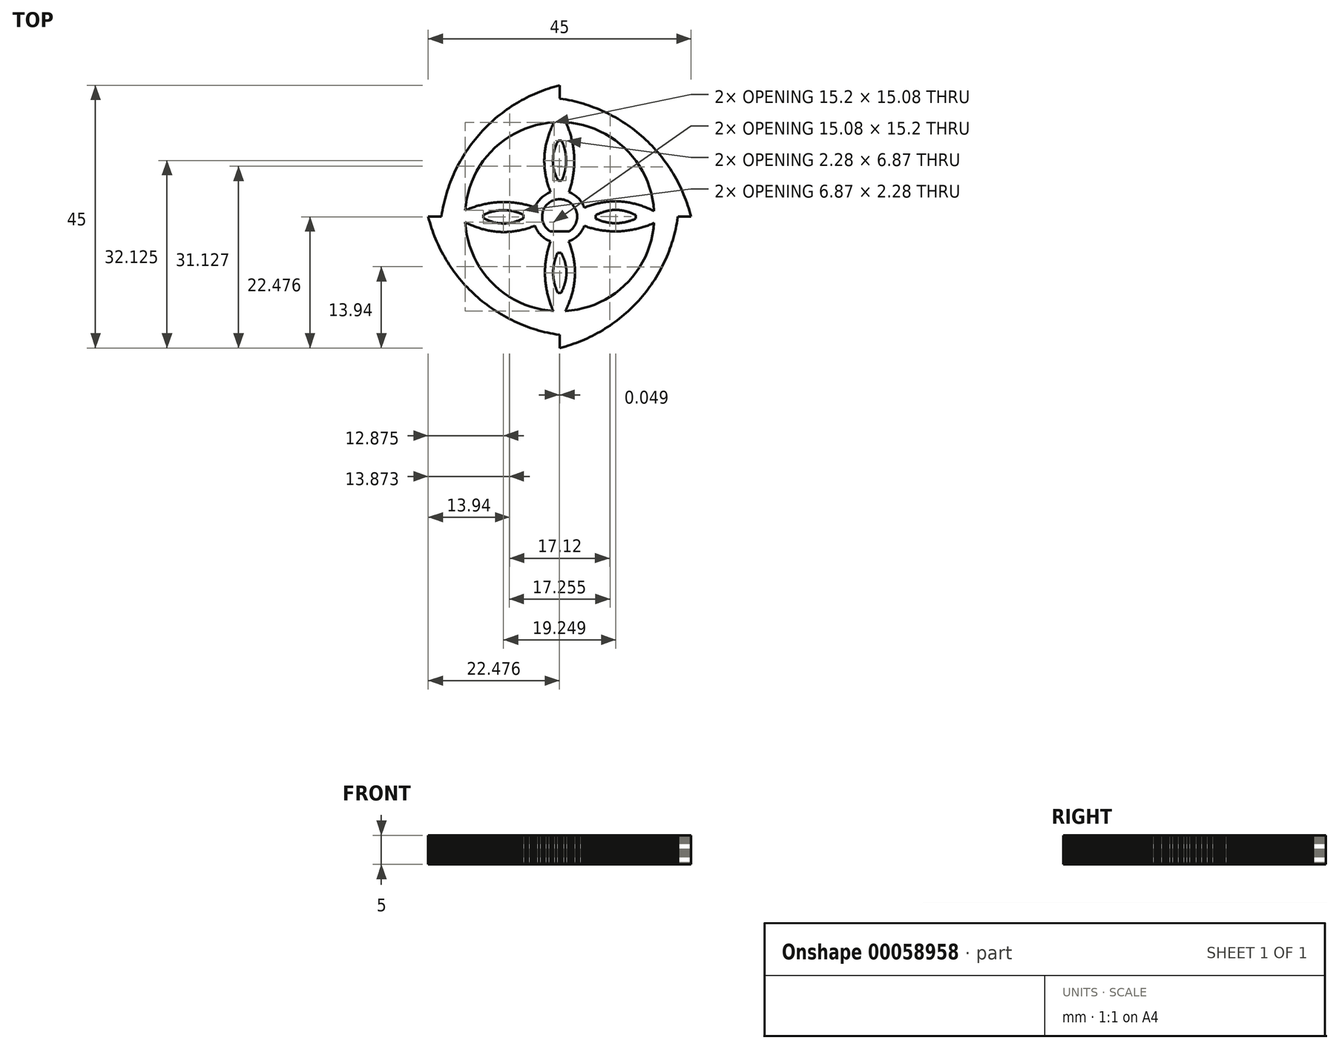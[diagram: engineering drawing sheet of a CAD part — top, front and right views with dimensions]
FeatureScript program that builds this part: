
annotation { "Feature Type Name" : "Feature", "Feature Type Description" : "" }
export const myFeature = defineFeature(function(context is Context, id is Id, definition is map)
    precondition{}
    {
        {
            var Q0;
            Q0=qCreatedBy(makeId("Top.planeOp"),FACE);
            var sketch = newSketch(context, id + "F0", { "sketchPlane" : qUnion([Q0])});
            skLineSegment(sketch, "E0", {"start": v(0, 22.5) * mm, "end": v(-0.48, 22.37) * mm});
            skLineSegment(sketch, "E1", {"start": v(-0.48, 22.37) * mm, "end": v(-0.97, 22.24) * mm});
            skLineSegment(sketch, "E2", {"start": v(-0.97, 22.24) * mm, "end": v(-1.44, 22.1) * mm});
            skLineSegment(sketch, "E3", {"start": v(-1.44, 22.1) * mm, "end": v(-1.92, 21.94) * mm});
            skLineSegment(sketch, "E4", {"start": v(-1.92, 21.94) * mm, "end": v(-2.4, 21.78) * mm});
            skLineSegment(sketch, "E5", {"start": v(-2.4, 21.78) * mm, "end": v(-2.86, 21.61) * mm});
            skLineSegment(sketch, "E6", {"start": v(-2.86, 21.61) * mm, "end": v(-3.33, 21.43) * mm});
            skLineSegment(sketch, "E7", {"start": v(-3.33, 21.43) * mm, "end": v(-3.8, 21.24) * mm});
            skLineSegment(sketch, "E8", {"start": v(-3.8, 21.24) * mm, "end": v(-4.25, 21.05) * mm});
            skLineSegment(sketch, "E9", {"start": v(-4.25, 21.05) * mm, "end": v(-4.71, 20.84) * mm});
            skLineSegment(sketch, "E10", {"start": v(-4.71, 20.84) * mm, "end": v(-5.16, 20.63) * mm});
            skLineSegment(sketch, "E11", {"start": v(-5.16, 20.63) * mm, "end": v(-5.61, 20.41) * mm});
            skLineSegment(sketch, "E12", {"start": v(-5.61, 20.41) * mm, "end": v(-6.06, 20.18) * mm});
            skLineSegment(sketch, "E13", {"start": v(-6.06, 20.18) * mm, "end": v(-6.5, 19.94) * mm});
            skLineSegment(sketch, "E14", {"start": v(-6.5, 19.94) * mm, "end": v(-6.93, 19.7) * mm});
            skLineSegment(sketch, "E15", {"start": v(-6.93, 19.7) * mm, "end": v(-7.36, 19.44) * mm});
            skLineSegment(sketch, "E16", {"start": v(-7.36, 19.44) * mm, "end": v(-7.79, 19.18) * mm});
            skLineSegment(sketch, "E17", {"start": v(-7.79, 19.18) * mm, "end": v(-8.2, 18.91) * mm});
            skLineSegment(sketch, "E18", {"start": v(-8.2, 18.91) * mm, "end": v(-8.63, 18.64) * mm});
            skLineSegment(sketch, "E19", {"start": v(-8.63, 18.64) * mm, "end": v(-9.04, 18.35) * mm});
            skLineSegment(sketch, "E20", {"start": v(-9.04, 18.35) * mm, "end": v(-9.44, 18.06) * mm});
            skLineSegment(sketch, "E21", {"start": v(-9.44, 18.06) * mm, "end": v(-9.84, 17.76) * mm});
            skLineSegment(sketch, "E22", {"start": v(-9.84, 17.76) * mm, "end": v(-10.24, 17.45) * mm});
            skLineSegment(sketch, "E23", {"start": v(-10.24, 17.45) * mm, "end": v(-10.63, 17.14) * mm});
            skLineSegment(sketch, "E24", {"start": v(-10.63, 17.14) * mm, "end": v(-11.01, 16.82) * mm});
            skLineSegment(sketch, "E25", {"start": v(-11.01, 16.82) * mm, "end": v(-11.39, 16.5) * mm});
            skLineSegment(sketch, "E26", {"start": v(-11.39, 16.5) * mm, "end": v(-11.76, 16.16) * mm});
            skLineSegment(sketch, "E27", {"start": v(-11.76, 16.16) * mm, "end": v(-12.12, 15.81) * mm});
            skLineSegment(sketch, "E28", {"start": v(-12.12, 15.81) * mm, "end": v(-12.48, 15.47) * mm});
            skLineSegment(sketch, "E29", {"start": v(-12.48, 15.47) * mm, "end": v(-12.83, 15.11) * mm});
            skLineSegment(sketch, "E30", {"start": v(-12.83, 15.11) * mm, "end": v(-13.18, 14.75) * mm});
            skLineSegment(sketch, "E31", {"start": v(-13.18, 14.75) * mm, "end": v(-13.52, 14.38) * mm});
            skLineSegment(sketch, "E32", {"start": v(-13.52, 14.38) * mm, "end": v(-13.85, 14) * mm});
            skLineSegment(sketch, "E33", {"start": v(-13.85, 14) * mm, "end": v(-14.17, 13.63) * mm});
            skLineSegment(sketch, "E34", {"start": v(-14.17, 13.63) * mm, "end": v(-14.5, 13.24) * mm});
            skLineSegment(sketch, "E35", {"start": v(-14.5, 13.24) * mm, "end": v(-14.8, 12.85) * mm});
            skLineSegment(sketch, "E36", {"start": v(-14.8, 12.85) * mm, "end": v(-15.1, 12.45) * mm});
            skLineSegment(sketch, "E37", {"start": v(-15.1, 12.45) * mm, "end": v(-15.4, 12.05) * mm});
            skLineSegment(sketch, "E38", {"start": v(-15.4, 12.05) * mm, "end": v(-15.7, 11.64) * mm});
            skLineSegment(sketch, "E39", {"start": v(-15.7, 11.64) * mm, "end": v(-15.97, 11.23) * mm});
            skLineSegment(sketch, "E40", {"start": v(-15.97, 11.23) * mm, "end": v(-16.25, 10.8) * mm});
            skLineSegment(sketch, "E41", {"start": v(-16.25, 10.8) * mm, "end": v(-16.51, 10.38) * mm});
            skLineSegment(sketch, "E42", {"start": v(-16.51, 10.38) * mm, "end": v(-16.77, 9.96) * mm});
            skLineSegment(sketch, "E43", {"start": v(-16.77, 9.96) * mm, "end": v(-17.02, 9.52) * mm});
            skLineSegment(sketch, "E44", {"start": v(-17.02, 9.52) * mm, "end": v(-17.26, 9.09) * mm});
            skLineSegment(sketch, "E45", {"start": v(-17.26, 9.09) * mm, "end": v(-17.5, 8.64) * mm});
            skLineSegment(sketch, "E46", {"start": v(-17.5, 8.64) * mm, "end": v(-17.72, 8.2) * mm});
            skLineSegment(sketch, "E47", {"start": v(-17.72, 8.2) * mm, "end": v(-17.94, 7.75) * mm});
            skLineSegment(sketch, "E48", {"start": v(-17.94, 7.75) * mm, "end": v(-18.14, 7.3) * mm});
            skLineSegment(sketch, "E49", {"start": v(-18.14, 7.3) * mm, "end": v(-18.35, 6.83) * mm});
            skLineSegment(sketch, "E50", {"start": v(-18.35, 6.83) * mm, "end": v(-18.54, 6.37) * mm});
            skLineSegment(sketch, "E51", {"start": v(-18.54, 6.37) * mm, "end": v(-18.72, 5.9) * mm});
            skLineSegment(sketch, "E52", {"start": v(-18.72, 5.9) * mm, "end": v(-18.9, 5.44) * mm});
            skLineSegment(sketch, "E53", {"start": v(-18.9, 5.44) * mm, "end": v(-19.06, 4.97) * mm});
            skLineSegment(sketch, "E54", {"start": v(-19.06, 4.97) * mm, "end": v(-19.22, 4.5) * mm});
            skLineSegment(sketch, "E55", {"start": v(-19.22, 4.5) * mm, "end": v(-19.37, 4.01) * mm});
            skLineSegment(sketch, "E56", {"start": v(-19.37, 4.01) * mm, "end": v(-19.5, 3.53) * mm});
            skLineSegment(sketch, "E57", {"start": v(-19.5, 3.53) * mm, "end": v(-19.64, 3.05) * mm});
            skLineSegment(sketch, "E58", {"start": v(-19.64, 3.05) * mm, "end": v(-19.76, 2.57) * mm});
            skLineSegment(sketch, "E59", {"start": v(-19.76, 2.57) * mm, "end": v(-19.87, 2.08) * mm});
            skLineSegment(sketch, "E60", {"start": v(-19.87, 2.08) * mm, "end": v(-19.98, 1.6) * mm});
            skLineSegment(sketch, "E61", {"start": v(-19.98, 1.6) * mm, "end": v(-20.07, 1.1) * mm});
            skLineSegment(sketch, "E62", {"start": v(-20.07, 1.1) * mm, "end": v(-20.16, 0.6) * mm});
            skLineSegment(sketch, "E63", {"start": v(-20.16, 0.6) * mm, "end": v(-20.23, 0.11) * mm});
            skLineSegment(sketch, "E64", {"start": v(-20.23, 0.11) * mm, "end": v(-20.25, 0) * mm});
            skLineSegment(sketch, "E65", {"start": v(-20.25, 0) * mm, "end": v(-22.5, 0) * mm});
            skLineSegment(sketch, "E66", {"start": v(-22.5, 0) * mm, "end": v(-22.37, -0.48) * mm});
            skLineSegment(sketch, "E67", {"start": v(-22.37, -0.48) * mm, "end": v(-22.24, -0.97) * mm});
            skLineSegment(sketch, "E68", {"start": v(-22.24, -0.97) * mm, "end": v(-22.1, -1.44) * mm});
            skLineSegment(sketch, "E69", {"start": v(-22.1, -1.44) * mm, "end": v(-21.94, -1.92) * mm});
            skLineSegment(sketch, "E70", {"start": v(-21.94, -1.92) * mm, "end": v(-21.78, -2.4) * mm});
            skLineSegment(sketch, "E71", {"start": v(-21.78, -2.4) * mm, "end": v(-21.61, -2.86) * mm});
            skLineSegment(sketch, "E72", {"start": v(-21.61, -2.86) * mm, "end": v(-21.43, -3.33) * mm});
            skLineSegment(sketch, "E73", {"start": v(-21.43, -3.33) * mm, "end": v(-21.24, -3.8) * mm});
            skLineSegment(sketch, "E74", {"start": v(-21.24, -3.8) * mm, "end": v(-21.05, -4.25) * mm});
            skLineSegment(sketch, "E75", {"start": v(-21.05, -4.25) * mm, "end": v(-20.84, -4.71) * mm});
            skLineSegment(sketch, "E76", {"start": v(-20.84, -4.71) * mm, "end": v(-20.63, -5.16) * mm});
            skLineSegment(sketch, "E77", {"start": v(-20.63, -5.16) * mm, "end": v(-20.41, -5.61) * mm});
            skLineSegment(sketch, "E78", {"start": v(-20.41, -5.61) * mm, "end": v(-20.18, -6.06) * mm});
            skLineSegment(sketch, "E79", {"start": v(-20.18, -6.06) * mm, "end": v(-19.94, -6.5) * mm});
            skLineSegment(sketch, "E80", {"start": v(-19.94, -6.5) * mm, "end": v(-19.7, -6.93) * mm});
            skLineSegment(sketch, "E81", {"start": v(-19.7, -6.93) * mm, "end": v(-19.44, -7.36) * mm});
            skLineSegment(sketch, "E82", {"start": v(-19.44, -7.36) * mm, "end": v(-19.18, -7.79) * mm});
            skLineSegment(sketch, "E83", {"start": v(-19.18, -7.79) * mm, "end": v(-18.91, -8.2) * mm});
            skLineSegment(sketch, "E84", {"start": v(-18.91, -8.2) * mm, "end": v(-18.64, -8.63) * mm});
            skLineSegment(sketch, "E85", {"start": v(-18.64, -8.63) * mm, "end": v(-18.35, -9.04) * mm});
            skLineSegment(sketch, "E86", {"start": v(-18.35, -9.04) * mm, "end": v(-18.06, -9.44) * mm});
            skLineSegment(sketch, "E87", {"start": v(-18.06, -9.44) * mm, "end": v(-17.76, -9.84) * mm});
            skLineSegment(sketch, "E88", {"start": v(-17.76, -9.84) * mm, "end": v(-17.45, -10.24) * mm});
            skLineSegment(sketch, "E89", {"start": v(-17.45, -10.24) * mm, "end": v(-17.14, -10.63) * mm});
            skLineSegment(sketch, "E90", {"start": v(-17.14, -10.63) * mm, "end": v(-16.82, -11.01) * mm});
            skLineSegment(sketch, "E91", {"start": v(-16.82, -11.01) * mm, "end": v(-16.5, -11.39) * mm});
            skLineSegment(sketch, "E92", {"start": v(-16.5, -11.39) * mm, "end": v(-16.16, -11.76) * mm});
            skLineSegment(sketch, "E93", {"start": v(-16.16, -11.76) * mm, "end": v(-15.81, -12.12) * mm});
            skLineSegment(sketch, "E94", {"start": v(-15.81, -12.12) * mm, "end": v(-15.47, -12.48) * mm});
            skLineSegment(sketch, "E95", {"start": v(-15.47, -12.48) * mm, "end": v(-15.11, -12.83) * mm});
            skLineSegment(sketch, "E96", {"start": v(-15.11, -12.83) * mm, "end": v(-14.75, -13.18) * mm});
            skLineSegment(sketch, "E97", {"start": v(-14.75, -13.18) * mm, "end": v(-14.38, -13.52) * mm});
            skLineSegment(sketch, "E98", {"start": v(-14.38, -13.52) * mm, "end": v(-14, -13.85) * mm});
            skLineSegment(sketch, "E99", {"start": v(-14, -13.85) * mm, "end": v(-13.63, -14.17) * mm});
            skLineSegment(sketch, "E100", {"start": v(-13.63, -14.17) * mm, "end": v(-13.24, -14.5) * mm});
            skLineSegment(sketch, "E101", {"start": v(-13.24, -14.5) * mm, "end": v(-12.85, -14.8) * mm});
            skLineSegment(sketch, "E102", {"start": v(-12.85, -14.8) * mm, "end": v(-12.45, -15.1) * mm});
            skLineSegment(sketch, "E103", {"start": v(-12.45, -15.1) * mm, "end": v(-12.05, -15.4) * mm});
            skLineSegment(sketch, "E104", {"start": v(-12.05, -15.4) * mm, "end": v(-11.64, -15.7) * mm});
            skLineSegment(sketch, "E105", {"start": v(-11.64, -15.7) * mm, "end": v(-11.23, -15.97) * mm});
            skLineSegment(sketch, "E106", {"start": v(-11.23, -15.97) * mm, "end": v(-10.8, -16.25) * mm});
            skLineSegment(sketch, "E107", {"start": v(-10.8, -16.25) * mm, "end": v(-10.38, -16.51) * mm});
            skLineSegment(sketch, "E108", {"start": v(-10.38, -16.51) * mm, "end": v(-9.96, -16.77) * mm});
            skLineSegment(sketch, "E109", {"start": v(-9.96, -16.77) * mm, "end": v(-9.52, -17.02) * mm});
            skLineSegment(sketch, "E110", {"start": v(-9.52, -17.02) * mm, "end": v(-9.09, -17.26) * mm});
            skLineSegment(sketch, "E111", {"start": v(-9.09, -17.26) * mm, "end": v(-8.64, -17.5) * mm});
            skLineSegment(sketch, "E112", {"start": v(-8.64, -17.5) * mm, "end": v(-8.2, -17.72) * mm});
            skLineSegment(sketch, "E113", {"start": v(-8.2, -17.72) * mm, "end": v(-7.75, -17.94) * mm});
            skLineSegment(sketch, "E114", {"start": v(-7.75, -17.94) * mm, "end": v(-7.3, -18.14) * mm});
            skLineSegment(sketch, "E115", {"start": v(-7.3, -18.14) * mm, "end": v(-6.83, -18.35) * mm});
            skLineSegment(sketch, "E116", {"start": v(-6.83, -18.35) * mm, "end": v(-6.37, -18.54) * mm});
            skLineSegment(sketch, "E117", {"start": v(-6.37, -18.54) * mm, "end": v(-5.9, -18.72) * mm});
            skLineSegment(sketch, "E118", {"start": v(-5.9, -18.72) * mm, "end": v(-5.44, -18.9) * mm});
            skLineSegment(sketch, "E119", {"start": v(-5.44, -18.9) * mm, "end": v(-4.97, -19.06) * mm});
            skLineSegment(sketch, "E120", {"start": v(-4.97, -19.06) * mm, "end": v(-4.5, -19.22) * mm});
            skLineSegment(sketch, "E121", {"start": v(-4.5, -19.22) * mm, "end": v(-4.01, -19.37) * mm});
            skLineSegment(sketch, "E122", {"start": v(-4.01, -19.37) * mm, "end": v(-3.53, -19.5) * mm});
            skLineSegment(sketch, "E123", {"start": v(-3.53, -19.5) * mm, "end": v(-3.05, -19.64) * mm});
            skLineSegment(sketch, "E124", {"start": v(-3.05, -19.64) * mm, "end": v(-2.57, -19.76) * mm});
            skLineSegment(sketch, "E125", {"start": v(-2.57, -19.76) * mm, "end": v(-2.08, -19.87) * mm});
            skLineSegment(sketch, "E126", {"start": v(-2.08, -19.87) * mm, "end": v(-1.6, -19.98) * mm});
            skLineSegment(sketch, "E127", {"start": v(-1.6, -19.98) * mm, "end": v(-1.1, -20.07) * mm});
            skLineSegment(sketch, "E128", {"start": v(-1.1, -20.07) * mm, "end": v(-0.6, -20.16) * mm});
            skLineSegment(sketch, "E129", {"start": v(-0.6, -20.16) * mm, "end": v(-0.11, -20.23) * mm});
            skLineSegment(sketch, "E130", {"start": v(-0.11, -20.23) * mm, "end": v(0, -20.25) * mm});
            skLineSegment(sketch, "E131", {"start": v(0, -20.25) * mm, "end": v(0, -22.5) * mm});
            skLineSegment(sketch, "E132", {"start": v(0, -22.5) * mm, "end": v(0.48, -22.37) * mm});
            skLineSegment(sketch, "E133", {"start": v(0.48, -22.37) * mm, "end": v(0.97, -22.24) * mm});
            skLineSegment(sketch, "E134", {"start": v(0.97, -22.24) * mm, "end": v(1.44, -22.1) * mm});
            skLineSegment(sketch, "E135", {"start": v(1.44, -22.1) * mm, "end": v(1.92, -21.94) * mm});
            skLineSegment(sketch, "E136", {"start": v(1.92, -21.94) * mm, "end": v(2.4, -21.78) * mm});
            skLineSegment(sketch, "E137", {"start": v(2.4, -21.78) * mm, "end": v(2.86, -21.61) * mm});
            skLineSegment(sketch, "E138", {"start": v(2.86, -21.61) * mm, "end": v(3.33, -21.43) * mm});
            skLineSegment(sketch, "E139", {"start": v(3.33, -21.43) * mm, "end": v(3.8, -21.24) * mm});
            skLineSegment(sketch, "E140", {"start": v(3.8, -21.24) * mm, "end": v(4.25, -21.05) * mm});
            skLineSegment(sketch, "E141", {"start": v(4.25, -21.05) * mm, "end": v(4.71, -20.84) * mm});
            skLineSegment(sketch, "E142", {"start": v(4.71, -20.84) * mm, "end": v(5.16, -20.63) * mm});
            skLineSegment(sketch, "E143", {"start": v(5.16, -20.63) * mm, "end": v(5.61, -20.41) * mm});
            skLineSegment(sketch, "E144", {"start": v(5.61, -20.41) * mm, "end": v(6.06, -20.18) * mm});
            skLineSegment(sketch, "E145", {"start": v(6.06, -20.18) * mm, "end": v(6.5, -19.94) * mm});
            skLineSegment(sketch, "E146", {"start": v(6.5, -19.94) * mm, "end": v(6.93, -19.7) * mm});
            skLineSegment(sketch, "E147", {"start": v(6.93, -19.7) * mm, "end": v(7.36, -19.44) * mm});
            skLineSegment(sketch, "E148", {"start": v(7.36, -19.44) * mm, "end": v(7.79, -19.18) * mm});
            skLineSegment(sketch, "E149", {"start": v(7.79, -19.18) * mm, "end": v(8.2, -18.91) * mm});
            skLineSegment(sketch, "E150", {"start": v(8.2, -18.91) * mm, "end": v(8.63, -18.64) * mm});
            skLineSegment(sketch, "E151", {"start": v(8.63, -18.64) * mm, "end": v(9.04, -18.35) * mm});
            skLineSegment(sketch, "E152", {"start": v(9.04, -18.35) * mm, "end": v(9.44, -18.06) * mm});
            skLineSegment(sketch, "E153", {"start": v(9.44, -18.06) * mm, "end": v(9.84, -17.76) * mm});
            skLineSegment(sketch, "E154", {"start": v(9.84, -17.76) * mm, "end": v(10.24, -17.45) * mm});
            skLineSegment(sketch, "E155", {"start": v(10.24, -17.45) * mm, "end": v(10.63, -17.14) * mm});
            skLineSegment(sketch, "E156", {"start": v(10.63, -17.14) * mm, "end": v(11.01, -16.82) * mm});
            skLineSegment(sketch, "E157", {"start": v(11.01, -16.82) * mm, "end": v(11.39, -16.5) * mm});
            skLineSegment(sketch, "E158", {"start": v(11.39, -16.5) * mm, "end": v(11.76, -16.16) * mm});
            skLineSegment(sketch, "E159", {"start": v(11.76, -16.16) * mm, "end": v(12.12, -15.81) * mm});
            skLineSegment(sketch, "E160", {"start": v(12.12, -15.81) * mm, "end": v(12.48, -15.47) * mm});
            skLineSegment(sketch, "E161", {"start": v(12.48, -15.47) * mm, "end": v(12.83, -15.11) * mm});
            skLineSegment(sketch, "E162", {"start": v(12.83, -15.11) * mm, "end": v(13.18, -14.75) * mm});
            skLineSegment(sketch, "E163", {"start": v(13.18, -14.75) * mm, "end": v(13.52, -14.38) * mm});
            skLineSegment(sketch, "E164", {"start": v(13.52, -14.38) * mm, "end": v(13.85, -14) * mm});
            skLineSegment(sketch, "E165", {"start": v(13.85, -14) * mm, "end": v(14.17, -13.63) * mm});
            skLineSegment(sketch, "E166", {"start": v(14.17, -13.63) * mm, "end": v(14.5, -13.24) * mm});
            skLineSegment(sketch, "E167", {"start": v(14.5, -13.24) * mm, "end": v(14.8, -12.85) * mm});
            skLineSegment(sketch, "E168", {"start": v(14.8, -12.85) * mm, "end": v(15.1, -12.45) * mm});
            skLineSegment(sketch, "E169", {"start": v(15.1, -12.45) * mm, "end": v(15.4, -12.05) * mm});
            skLineSegment(sketch, "E170", {"start": v(15.4, -12.05) * mm, "end": v(15.7, -11.64) * mm});
            skLineSegment(sketch, "E171", {"start": v(15.7, -11.64) * mm, "end": v(15.97, -11.23) * mm});
            skLineSegment(sketch, "E172", {"start": v(15.97, -11.23) * mm, "end": v(16.25, -10.8) * mm});
            skLineSegment(sketch, "E173", {"start": v(16.25, -10.8) * mm, "end": v(16.51, -10.38) * mm});
            skLineSegment(sketch, "E174", {"start": v(16.51, -10.38) * mm, "end": v(16.77, -9.96) * mm});
            skLineSegment(sketch, "E175", {"start": v(16.77, -9.96) * mm, "end": v(17.02, -9.52) * mm});
            skLineSegment(sketch, "E176", {"start": v(17.02, -9.52) * mm, "end": v(17.26, -9.09) * mm});
            skLineSegment(sketch, "E177", {"start": v(17.26, -9.09) * mm, "end": v(17.5, -8.64) * mm});
            skLineSegment(sketch, "E178", {"start": v(17.5, -8.64) * mm, "end": v(17.72, -8.2) * mm});
            skLineSegment(sketch, "E179", {"start": v(17.72, -8.2) * mm, "end": v(17.94, -7.75) * mm});
            skLineSegment(sketch, "E180", {"start": v(17.94, -7.75) * mm, "end": v(18.14, -7.3) * mm});
            skLineSegment(sketch, "E181", {"start": v(18.14, -7.3) * mm, "end": v(18.35, -6.83) * mm});
            skLineSegment(sketch, "E182", {"start": v(18.35, -6.83) * mm, "end": v(18.54, -6.37) * mm});
            skLineSegment(sketch, "E183", {"start": v(18.54, -6.37) * mm, "end": v(18.72, -5.9) * mm});
            skLineSegment(sketch, "E184", {"start": v(18.72, -5.9) * mm, "end": v(18.9, -5.44) * mm});
            skLineSegment(sketch, "E185", {"start": v(18.9, -5.44) * mm, "end": v(19.06, -4.97) * mm});
            skLineSegment(sketch, "E186", {"start": v(19.06, -4.97) * mm, "end": v(19.22, -4.5) * mm});
            skLineSegment(sketch, "E187", {"start": v(19.22, -4.5) * mm, "end": v(19.37, -4.01) * mm});
            skLineSegment(sketch, "E188", {"start": v(19.37, -4.01) * mm, "end": v(19.5, -3.53) * mm});
            skLineSegment(sketch, "E189", {"start": v(19.5, -3.53) * mm, "end": v(19.64, -3.05) * mm});
            skLineSegment(sketch, "E190", {"start": v(19.64, -3.05) * mm, "end": v(19.76, -2.57) * mm});
            skLineSegment(sketch, "E191", {"start": v(19.76, -2.57) * mm, "end": v(19.87, -2.08) * mm});
            skLineSegment(sketch, "E192", {"start": v(19.87, -2.08) * mm, "end": v(19.98, -1.6) * mm});
            skLineSegment(sketch, "E193", {"start": v(19.98, -1.6) * mm, "end": v(20.07, -1.1) * mm});
            skLineSegment(sketch, "E194", {"start": v(20.07, -1.1) * mm, "end": v(20.16, -0.6) * mm});
            skLineSegment(sketch, "E195", {"start": v(20.16, -0.6) * mm, "end": v(20.23, -0.11) * mm});
            skLineSegment(sketch, "E196", {"start": v(20.23, -0.11) * mm, "end": v(20.25, 0) * mm});
            skLineSegment(sketch, "E197", {"start": v(20.25, 0) * mm, "end": v(22.5, 0) * mm});
            skLineSegment(sketch, "E198", {"start": v(22.5, 0) * mm, "end": v(22.37, 0.48) * mm});
            skLineSegment(sketch, "E199", {"start": v(22.37, 0.48) * mm, "end": v(22.24, 0.97) * mm});
            skLineSegment(sketch, "E200", {"start": v(22.24, 0.97) * mm, "end": v(22.1, 1.44) * mm});
            skLineSegment(sketch, "E201", {"start": v(22.1, 1.44) * mm, "end": v(21.94, 1.92) * mm});
            skLineSegment(sketch, "E202", {"start": v(21.94, 1.92) * mm, "end": v(21.78, 2.4) * mm});
            skLineSegment(sketch, "E203", {"start": v(21.78, 2.4) * mm, "end": v(21.61, 2.86) * mm});
            skLineSegment(sketch, "E204", {"start": v(21.61, 2.86) * mm, "end": v(21.43, 3.33) * mm});
            skLineSegment(sketch, "E205", {"start": v(21.43, 3.33) * mm, "end": v(21.24, 3.8) * mm});
            skLineSegment(sketch, "E206", {"start": v(21.24, 3.8) * mm, "end": v(21.05, 4.25) * mm});
            skLineSegment(sketch, "E207", {"start": v(21.05, 4.25) * mm, "end": v(20.84, 4.71) * mm});
            skLineSegment(sketch, "E208", {"start": v(20.84, 4.71) * mm, "end": v(20.63, 5.16) * mm});
            skLineSegment(sketch, "E209", {"start": v(20.63, 5.16) * mm, "end": v(20.41, 5.61) * mm});
            skLineSegment(sketch, "E210", {"start": v(20.41, 5.61) * mm, "end": v(20.18, 6.06) * mm});
            skLineSegment(sketch, "E211", {"start": v(20.18, 6.06) * mm, "end": v(19.94, 6.5) * mm});
            skLineSegment(sketch, "E212", {"start": v(19.94, 6.5) * mm, "end": v(19.7, 6.93) * mm});
            skLineSegment(sketch, "E213", {"start": v(19.7, 6.93) * mm, "end": v(19.44, 7.36) * mm});
            skLineSegment(sketch, "E214", {"start": v(19.44, 7.36) * mm, "end": v(19.18, 7.79) * mm});
            skLineSegment(sketch, "E215", {"start": v(19.18, 7.79) * mm, "end": v(18.91, 8.2) * mm});
            skLineSegment(sketch, "E216", {"start": v(18.91, 8.2) * mm, "end": v(18.64, 8.63) * mm});
            skLineSegment(sketch, "E217", {"start": v(18.64, 8.63) * mm, "end": v(18.35, 9.04) * mm});
            skLineSegment(sketch, "E218", {"start": v(18.35, 9.04) * mm, "end": v(18.06, 9.44) * mm});
            skLineSegment(sketch, "E219", {"start": v(18.06, 9.44) * mm, "end": v(17.76, 9.84) * mm});
            skLineSegment(sketch, "E220", {"start": v(17.76, 9.84) * mm, "end": v(17.45, 10.24) * mm});
            skLineSegment(sketch, "E221", {"start": v(17.45, 10.24) * mm, "end": v(17.14, 10.63) * mm});
            skLineSegment(sketch, "E222", {"start": v(17.14, 10.63) * mm, "end": v(16.82, 11.01) * mm});
            skLineSegment(sketch, "E223", {"start": v(16.82, 11.01) * mm, "end": v(16.5, 11.39) * mm});
            skLineSegment(sketch, "E224", {"start": v(16.5, 11.39) * mm, "end": v(16.16, 11.76) * mm});
            skLineSegment(sketch, "E225", {"start": v(16.16, 11.76) * mm, "end": v(15.81, 12.12) * mm});
            skLineSegment(sketch, "E226", {"start": v(15.81, 12.12) * mm, "end": v(15.47, 12.48) * mm});
            skLineSegment(sketch, "E227", {"start": v(15.47, 12.48) * mm, "end": v(15.11, 12.83) * mm});
            skLineSegment(sketch, "E228", {"start": v(15.11, 12.83) * mm, "end": v(14.75, 13.18) * mm});
            skLineSegment(sketch, "E229", {"start": v(14.75, 13.18) * mm, "end": v(14.38, 13.52) * mm});
            skLineSegment(sketch, "E230", {"start": v(14.38, 13.52) * mm, "end": v(14, 13.85) * mm});
            skLineSegment(sketch, "E231", {"start": v(14, 13.85) * mm, "end": v(13.63, 14.17) * mm});
            skLineSegment(sketch, "E232", {"start": v(13.63, 14.17) * mm, "end": v(13.24, 14.5) * mm});
            skLineSegment(sketch, "E233", {"start": v(13.24, 14.5) * mm, "end": v(12.85, 14.8) * mm});
            skLineSegment(sketch, "E234", {"start": v(12.85, 14.8) * mm, "end": v(12.45, 15.1) * mm});
            skLineSegment(sketch, "E235", {"start": v(12.45, 15.1) * mm, "end": v(12.05, 15.4) * mm});
            skLineSegment(sketch, "E236", {"start": v(12.05, 15.4) * mm, "end": v(11.64, 15.7) * mm});
            skLineSegment(sketch, "E237", {"start": v(11.64, 15.7) * mm, "end": v(11.23, 15.97) * mm});
            skLineSegment(sketch, "E238", {"start": v(11.23, 15.97) * mm, "end": v(10.8, 16.25) * mm});
            skLineSegment(sketch, "E239", {"start": v(10.8, 16.25) * mm, "end": v(10.38, 16.51) * mm});
            skLineSegment(sketch, "E240", {"start": v(10.38, 16.51) * mm, "end": v(9.96, 16.77) * mm});
            skLineSegment(sketch, "E241", {"start": v(9.96, 16.77) * mm, "end": v(9.52, 17.02) * mm});
            skLineSegment(sketch, "E242", {"start": v(9.52, 17.02) * mm, "end": v(9.09, 17.26) * mm});
            skLineSegment(sketch, "E243", {"start": v(9.09, 17.26) * mm, "end": v(8.64, 17.5) * mm});
            skLineSegment(sketch, "E244", {"start": v(8.64, 17.5) * mm, "end": v(8.2, 17.72) * mm});
            skLineSegment(sketch, "E245", {"start": v(8.2, 17.72) * mm, "end": v(7.75, 17.94) * mm});
            skLineSegment(sketch, "E246", {"start": v(7.75, 17.94) * mm, "end": v(7.3, 18.14) * mm});
            skLineSegment(sketch, "E247", {"start": v(7.3, 18.14) * mm, "end": v(6.83, 18.35) * mm});
            skLineSegment(sketch, "E248", {"start": v(6.83, 18.35) * mm, "end": v(6.37, 18.54) * mm});
            skLineSegment(sketch, "E249", {"start": v(6.37, 18.54) * mm, "end": v(5.9, 18.72) * mm});
            skLineSegment(sketch, "E250", {"start": v(5.9, 18.72) * mm, "end": v(5.44, 18.9) * mm});
            skLineSegment(sketch, "E251", {"start": v(5.44, 18.9) * mm, "end": v(4.97, 19.06) * mm});
            skLineSegment(sketch, "E252", {"start": v(4.97, 19.06) * mm, "end": v(4.5, 19.22) * mm});
            skLineSegment(sketch, "E253", {"start": v(4.5, 19.22) * mm, "end": v(4.01, 19.37) * mm});
            skLineSegment(sketch, "E254", {"start": v(4.01, 19.37) * mm, "end": v(3.53, 19.5) * mm});
            skLineSegment(sketch, "E255", {"start": v(3.53, 19.5) * mm, "end": v(3.05, 19.64) * mm});
            skLineSegment(sketch, "E256", {"start": v(3.05, 19.64) * mm, "end": v(2.57, 19.76) * mm});
            skLineSegment(sketch, "E257", {"start": v(2.57, 19.76) * mm, "end": v(2.08, 19.87) * mm});
            skLineSegment(sketch, "E258", {"start": v(2.08, 19.87) * mm, "end": v(1.6, 19.98) * mm});
            skLineSegment(sketch, "E259", {"start": v(1.6, 19.98) * mm, "end": v(1.1, 20.07) * mm});
            skLineSegment(sketch, "E260", {"start": v(1.1, 20.07) * mm, "end": v(0.6, 20.16) * mm});
            skLineSegment(sketch, "E261", {"start": v(0.6, 20.16) * mm, "end": v(0.11, 20.23) * mm});
            skLineSegment(sketch, "E262", {"start": v(0.11, 20.23) * mm, "end": v(0, 20.25) * mm});
            skLineSegment(sketch, "E263", {"start": v(0, 20.25) * mm, "end": v(0, 22.5) * mm});
            skLineSegment(sketch, "E264", {"start": v(-16.04, 1.14) * mm, "end": v(-15.83, 1.23) * mm});
            skLineSegment(sketch, "E265", {"start": v(-15.83, 1.23) * mm, "end": v(-15.61, 1.32) * mm});
            skLineSegment(sketch, "E266", {"start": v(-15.61, 1.32) * mm, "end": v(-15.4, 1.4) * mm});
            skLineSegment(sketch, "E267", {"start": v(-15.4, 1.4) * mm, "end": v(-15.19, 1.48) * mm});
            skLineSegment(sketch, "E268", {"start": v(-15.19, 1.48) * mm, "end": v(-14.97, 1.56) * mm});
            skLineSegment(sketch, "E269", {"start": v(-14.97, 1.56) * mm, "end": v(-14.76, 1.63) * mm});
            skLineSegment(sketch, "E270", {"start": v(-14.76, 1.63) * mm, "end": v(-14.54, 1.7) * mm});
            skLineSegment(sketch, "E271", {"start": v(-14.54, 1.7) * mm, "end": v(-14.33, 1.77) * mm});
            skLineSegment(sketch, "E272", {"start": v(-14.33, 1.77) * mm, "end": v(-14.11, 1.84) * mm});
            skLineSegment(sketch, "E273", {"start": v(-14.11, 1.84) * mm, "end": v(-13.9, 1.9) * mm});
            skLineSegment(sketch, "E274", {"start": v(-13.9, 1.9) * mm, "end": v(-13.68, 1.96) * mm});
            skLineSegment(sketch, "E275", {"start": v(-13.68, 1.96) * mm, "end": v(-13.47, 2.01) * mm});
            skLineSegment(sketch, "E276", {"start": v(-13.47, 2.01) * mm, "end": v(-13.25, 2.07) * mm});
            skLineSegment(sketch, "E277", {"start": v(-13.25, 2.07) * mm, "end": v(-13.04, 2.12) * mm});
            skLineSegment(sketch, "E278", {"start": v(-13.04, 2.12) * mm, "end": v(-12.82, 2.17) * mm});
            skLineSegment(sketch, "E279", {"start": v(-12.82, 2.17) * mm, "end": v(-12.6, 2.21) * mm});
            skLineSegment(sketch, "E280", {"start": v(-12.6, 2.21) * mm, "end": v(-12.39, 2.25) * mm});
            skLineSegment(sketch, "E281", {"start": v(-12.39, 2.25) * mm, "end": v(-12.17, 2.3) * mm});
            skLineSegment(sketch, "E282", {"start": v(-12.17, 2.3) * mm, "end": v(-11.96, 2.33) * mm});
            skLineSegment(sketch, "E283", {"start": v(-11.96, 2.33) * mm, "end": v(-11.74, 2.36) * mm});
            skLineSegment(sketch, "E284", {"start": v(-11.74, 2.36) * mm, "end": v(-11.52, 2.39) * mm});
            skLineSegment(sketch, "E285", {"start": v(-11.52, 2.39) * mm, "end": v(-11.3, 2.41) * mm});
            skLineSegment(sketch, "E286", {"start": v(-11.3, 2.41) * mm, "end": v(-11.09, 2.44) * mm});
            skLineSegment(sketch, "E287", {"start": v(-11.09, 2.44) * mm, "end": v(-10.87, 2.46) * mm});
            skLineSegment(sketch, "E288", {"start": v(-10.87, 2.46) * mm, "end": v(-10.65, 2.47) * mm});
            skLineSegment(sketch, "E289", {"start": v(-10.65, 2.47) * mm, "end": v(-10.43, 2.49) * mm});
            skLineSegment(sketch, "E290", {"start": v(-10.43, 2.49) * mm, "end": v(-10.22, 2.5) * mm});
            skLineSegment(sketch, "E291", {"start": v(-10.22, 2.5) * mm, "end": v(-10, 2.5) * mm});
            skLineSegment(sketch, "E292", {"start": v(-10, 2.5) * mm, "end": v(-9.78, 2.51) * mm});
            skLineSegment(sketch, "E293", {"start": v(-9.78, 2.51) * mm, "end": v(-9.56, 2.51) * mm});
            skLineSegment(sketch, "E294", {"start": v(-9.56, 2.51) * mm, "end": v(-9.34, 2.51) * mm});
            skLineSegment(sketch, "E295", {"start": v(-9.34, 2.51) * mm, "end": v(-9.13, 2.5) * mm});
            skLineSegment(sketch, "E296", {"start": v(-9.13, 2.5) * mm, "end": v(-8.91, 2.5) * mm});
            skLineSegment(sketch, "E297", {"start": v(-8.91, 2.5) * mm, "end": v(-8.7, 2.49) * mm});
            skLineSegment(sketch, "E298", {"start": v(-8.7, 2.49) * mm, "end": v(-8.48, 2.47) * mm});
            skLineSegment(sketch, "E299", {"start": v(-8.48, 2.47) * mm, "end": v(-8.27, 2.46) * mm});
            skLineSegment(sketch, "E300", {"start": v(-8.27, 2.46) * mm, "end": v(-8.05, 2.44) * mm});
            skLineSegment(sketch, "E301", {"start": v(-8.05, 2.44) * mm, "end": v(-7.84, 2.42) * mm});
            skLineSegment(sketch, "E302", {"start": v(-7.84, 2.42) * mm, "end": v(-7.62, 2.4) * mm});
            skLineSegment(sketch, "E303", {"start": v(-7.62, 2.4) * mm, "end": v(-7.4, 2.36) * mm});
            skLineSegment(sketch, "E304", {"start": v(-7.4, 2.36) * mm, "end": v(-7.2, 2.33) * mm});
            skLineSegment(sketch, "E305", {"start": v(-7.2, 2.33) * mm, "end": v(-6.98, 2.3) * mm});
            skLineSegment(sketch, "E306", {"start": v(-6.98, 2.3) * mm, "end": v(-6.77, 2.26) * mm});
            skLineSegment(sketch, "E307", {"start": v(-6.77, 2.26) * mm, "end": v(-6.56, 2.22) * mm});
            skLineSegment(sketch, "E308", {"start": v(-6.56, 2.22) * mm, "end": v(-6.34, 2.18) * mm});
            skLineSegment(sketch, "E309", {"start": v(-6.34, 2.18) * mm, "end": v(-6.13, 2.13) * mm});
            skLineSegment(sketch, "E310", {"start": v(-6.13, 2.13) * mm, "end": v(-5.92, 2.08) * mm});
            skLineSegment(sketch, "E311", {"start": v(-5.92, 2.08) * mm, "end": v(-5.7, 2.03) * mm});
            skLineSegment(sketch, "E312", {"start": v(-5.7, 2.03) * mm, "end": v(-5.5, 1.97) * mm});
            skLineSegment(sketch, "E313", {"start": v(-5.5, 1.97) * mm, "end": v(-5.28, 1.92) * mm});
            skLineSegment(sketch, "E314", {"start": v(-5.28, 1.92) * mm, "end": v(-5.07, 1.85) * mm});
            skLineSegment(sketch, "E315", {"start": v(-5.07, 1.85) * mm, "end": v(-4.86, 1.8) * mm});
            skLineSegment(sketch, "E316", {"start": v(-4.86, 1.8) * mm, "end": v(-4.64, 1.72) * mm});
            skLineSegment(sketch, "E317", {"start": v(-4.64, 1.72) * mm, "end": v(-4.43, 1.66) * mm});
            skLineSegment(sketch, "E318", {"start": v(-4.43, 1.66) * mm, "end": v(-4.22, 1.58) * mm});
            skLineSegment(sketch, "E319", {"start": v(-4.22, 1.58) * mm, "end": v(-4.01, 1.5) * mm});
            skLineSegment(sketch, "E320", {"start": v(-4.01, 1.5) * mm, "end": v(-3.8, 1.43) * mm});
            skLineSegment(sketch, "E321", {"start": v(-3.8, 1.43) * mm, "end": v(-3.6, 1.35) * mm});
            skLineSegment(sketch, "E322", {"start": v(-3.6, 1.35) * mm, "end": v(-3.38, 1.26) * mm});
            skLineSegment(sketch, "E323", {"start": v(-3.38, 1.26) * mm, "end": v(-3.17, 1.18) * mm});
            skLineSegment(sketch, "E324", {"start": v(-3.17, 1.18) * mm, "end": v(-3.02, 1.12) * mm});
            skLineSegment(sketch, "E325", {"start": v(-3.02, 1.12) * mm, "end": v(-3, 1.19) * mm});
            skLineSegment(sketch, "E326", {"start": v(-3, 1.19) * mm, "end": v(-2.92, 1.37) * mm});
            skLineSegment(sketch, "E327", {"start": v(-2.92, 1.37) * mm, "end": v(-2.83, 1.55) * mm});
            skLineSegment(sketch, "E328", {"start": v(-2.83, 1.55) * mm, "end": v(-2.72, 1.73) * mm});
            skLineSegment(sketch, "E329", {"start": v(-2.72, 1.73) * mm, "end": v(-2.6, 1.9) * mm});
            skLineSegment(sketch, "E330", {"start": v(-2.6, 1.9) * mm, "end": v(-2.48, 2.06) * mm});
            skLineSegment(sketch, "E331", {"start": v(-2.48, 2.06) * mm, "end": v(-2.35, 2.2) * mm});
            skLineSegment(sketch, "E332", {"start": v(-2.35, 2.2) * mm, "end": v(-2.2, 2.35) * mm});
            skLineSegment(sketch, "E333", {"start": v(-2.2, 2.35) * mm, "end": v(-2.06, 2.48) * mm});
            skLineSegment(sketch, "E334", {"start": v(-2.06, 2.48) * mm, "end": v(-1.9, 2.6) * mm});
            skLineSegment(sketch, "E335", {"start": v(-1.9, 2.6) * mm, "end": v(-1.73, 2.72) * mm});
            skLineSegment(sketch, "E336", {"start": v(-1.73, 2.72) * mm, "end": v(-1.55, 2.83) * mm});
            skLineSegment(sketch, "E337", {"start": v(-1.55, 2.83) * mm, "end": v(-1.37, 2.92) * mm});
            skLineSegment(sketch, "E338", {"start": v(-1.37, 2.92) * mm, "end": v(-1.19, 3) * mm});
            skLineSegment(sketch, "E339", {"start": v(-1.19, 3) * mm, "end": v(-1.02, 3.06) * mm});
            skLineSegment(sketch, "E340", {"start": v(-1.02, 3.06) * mm, "end": v(-1.07, 3.17) * mm});
            skLineSegment(sketch, "E341", {"start": v(-1.07, 3.17) * mm, "end": v(-1.17, 3.38) * mm});
            skLineSegment(sketch, "E342", {"start": v(-1.17, 3.38) * mm, "end": v(-1.27, 3.6) * mm});
            skLineSegment(sketch, "E343", {"start": v(-1.27, 3.6) * mm, "end": v(-1.36, 3.8) * mm});
            skLineSegment(sketch, "E344", {"start": v(-1.36, 3.8) * mm, "end": v(-1.45, 4.01) * mm});
            skLineSegment(sketch, "E345", {"start": v(-1.45, 4.01) * mm, "end": v(-1.54, 4.22) * mm});
            skLineSegment(sketch, "E346", {"start": v(-1.54, 4.22) * mm, "end": v(-1.63, 4.43) * mm});
            skLineSegment(sketch, "E347", {"start": v(-1.63, 4.43) * mm, "end": v(-1.7, 4.64) * mm});
            skLineSegment(sketch, "E348", {"start": v(-1.7, 4.64) * mm, "end": v(-1.78, 4.86) * mm});
            skLineSegment(sketch, "E349", {"start": v(-1.78, 4.86) * mm, "end": v(-1.86, 5.07) * mm});
            skLineSegment(sketch, "E350", {"start": v(-1.86, 5.07) * mm, "end": v(-1.93, 5.28) * mm});
            skLineSegment(sketch, "E351", {"start": v(-1.93, 5.28) * mm, "end": v(-2, 5.5) * mm});
            skLineSegment(sketch, "E352", {"start": v(-2, 5.5) * mm, "end": v(-2.06, 5.7) * mm});
            skLineSegment(sketch, "E353", {"start": v(-2.06, 5.7) * mm, "end": v(-2.12, 5.92) * mm});
            skLineSegment(sketch, "E354", {"start": v(-2.12, 5.92) * mm, "end": v(-2.18, 6.13) * mm});
            skLineSegment(sketch, "E355", {"start": v(-2.18, 6.13) * mm, "end": v(-2.23, 6.34) * mm});
            skLineSegment(sketch, "E356", {"start": v(-2.23, 6.34) * mm, "end": v(-2.28, 6.56) * mm});
            skLineSegment(sketch, "E357", {"start": v(-2.28, 6.56) * mm, "end": v(-2.33, 6.77) * mm});
            skLineSegment(sketch, "E358", {"start": v(-2.33, 6.77) * mm, "end": v(-2.37, 6.98) * mm});
            skLineSegment(sketch, "E359", {"start": v(-2.37, 6.98) * mm, "end": v(-2.41, 7.2) * mm});
            skLineSegment(sketch, "E360", {"start": v(-2.41, 7.2) * mm, "end": v(-2.45, 7.4) * mm});
            skLineSegment(sketch, "E361", {"start": v(-2.45, 7.4) * mm, "end": v(-2.48, 7.62) * mm});
            skLineSegment(sketch, "E362", {"start": v(-2.48, 7.62) * mm, "end": v(-2.51, 7.84) * mm});
            skLineSegment(sketch, "E363", {"start": v(-2.51, 7.84) * mm, "end": v(-2.54, 8.05) * mm});
            skLineSegment(sketch, "E364", {"start": v(-2.54, 8.05) * mm, "end": v(-2.56, 8.27) * mm});
            skLineSegment(sketch, "E365", {"start": v(-2.56, 8.27) * mm, "end": v(-2.58, 8.48) * mm});
            skLineSegment(sketch, "E366", {"start": v(-2.58, 8.48) * mm, "end": v(-2.6, 8.7) * mm});
            skLineSegment(sketch, "E367", {"start": v(-2.6, 8.7) * mm, "end": v(-2.6, 8.91) * mm});
            skLineSegment(sketch, "E368", {"start": v(-2.6, 8.91) * mm, "end": v(-2.62, 9.13) * mm});
            skLineSegment(sketch, "E369", {"start": v(-2.62, 9.13) * mm, "end": v(-2.62, 9.34) * mm});
            skLineSegment(sketch, "E370", {"start": v(-2.62, 9.34) * mm, "end": v(-2.62, 9.56) * mm});
            skLineSegment(sketch, "E371", {"start": v(-2.62, 9.56) * mm, "end": v(-2.62, 9.78) * mm});
            skLineSegment(sketch, "E372", {"start": v(-2.62, 9.78) * mm, "end": v(-2.62, 10) * mm});
            skLineSegment(sketch, "E373", {"start": v(-2.62, 10) * mm, "end": v(-2.6, 10.22) * mm});
            skLineSegment(sketch, "E374", {"start": v(-2.6, 10.22) * mm, "end": v(-2.6, 10.43) * mm});
            skLineSegment(sketch, "E375", {"start": v(-2.6, 10.43) * mm, "end": v(-2.58, 10.65) * mm});
            skLineSegment(sketch, "E376", {"start": v(-2.58, 10.65) * mm, "end": v(-2.56, 10.87) * mm});
            skLineSegment(sketch, "E377", {"start": v(-2.56, 10.87) * mm, "end": v(-2.54, 11.09) * mm});
            skLineSegment(sketch, "E378", {"start": v(-2.54, 11.09) * mm, "end": v(-2.5, 11.3) * mm});
            skLineSegment(sketch, "E379", {"start": v(-2.5, 11.3) * mm, "end": v(-2.48, 11.52) * mm});
            skLineSegment(sketch, "E380", {"start": v(-2.48, 11.52) * mm, "end": v(-2.44, 11.74) * mm});
            skLineSegment(sketch, "E381", {"start": v(-2.44, 11.74) * mm, "end": v(-2.4, 11.96) * mm});
            skLineSegment(sketch, "E382", {"start": v(-2.4, 11.96) * mm, "end": v(-2.37, 12.17) * mm});
            skLineSegment(sketch, "E383", {"start": v(-2.37, 12.17) * mm, "end": v(-2.32, 12.39) * mm});
            skLineSegment(sketch, "E384", {"start": v(-2.32, 12.39) * mm, "end": v(-2.27, 12.6) * mm});
            skLineSegment(sketch, "E385", {"start": v(-2.27, 12.6) * mm, "end": v(-2.22, 12.82) * mm});
            skLineSegment(sketch, "E386", {"start": v(-2.22, 12.82) * mm, "end": v(-2.17, 13.04) * mm});
            skLineSegment(sketch, "E387", {"start": v(-2.17, 13.04) * mm, "end": v(-2.1, 13.25) * mm});
            skLineSegment(sketch, "E388", {"start": v(-2.1, 13.25) * mm, "end": v(-2.04, 13.47) * mm});
            skLineSegment(sketch, "E389", {"start": v(-2.04, 13.47) * mm, "end": v(-1.98, 13.68) * mm});
            skLineSegment(sketch, "E390", {"start": v(-1.98, 13.68) * mm, "end": v(-1.9, 13.9) * mm});
            skLineSegment(sketch, "E391", {"start": v(-1.9, 13.9) * mm, "end": v(-1.84, 14.11) * mm});
            skLineSegment(sketch, "E392", {"start": v(-1.84, 14.11) * mm, "end": v(-1.76, 14.33) * mm});
            skLineSegment(sketch, "E393", {"start": v(-1.76, 14.33) * mm, "end": v(-1.68, 14.54) * mm});
            skLineSegment(sketch, "E394", {"start": v(-1.68, 14.54) * mm, "end": v(-1.6, 14.76) * mm});
            skLineSegment(sketch, "E395", {"start": v(-1.6, 14.76) * mm, "end": v(-1.51, 14.97) * mm});
            skLineSegment(sketch, "E396", {"start": v(-1.51, 14.97) * mm, "end": v(-1.42, 15.19) * mm});
            skLineSegment(sketch, "E397", {"start": v(-1.42, 15.19) * mm, "end": v(-1.33, 15.4) * mm});
            skLineSegment(sketch, "E398", {"start": v(-1.33, 15.4) * mm, "end": v(-1.23, 15.61) * mm});
            skLineSegment(sketch, "E399", {"start": v(-1.23, 15.61) * mm, "end": v(-1.13, 15.83) * mm});
            skLineSegment(sketch, "E400", {"start": v(-1.13, 15.83) * mm, "end": v(-1.03, 16.04) * mm});
            skLineSegment(sketch, "E401", {"start": v(-1.03, 16.04) * mm, "end": v(-0.96, 16.17) * mm});
            skLineSegment(sketch, "E402", {"start": v(-0.96, 16.17) * mm, "end": v(-1.02, 16.17) * mm});
            skLineSegment(sketch, "E403", {"start": v(-1.02, 16.17) * mm, "end": v(-2.03, 16.07) * mm});
            skLineSegment(sketch, "E404", {"start": v(-2.03, 16.07) * mm, "end": v(-3.04, 15.91) * mm});
            skLineSegment(sketch, "E405", {"start": v(-3.04, 15.91) * mm, "end": v(-4.03, 15.69) * mm});
            skLineSegment(sketch, "E406", {"start": v(-4.03, 15.69) * mm, "end": v(-5, 15.4) * mm});
            skLineSegment(sketch, "E407", {"start": v(-5, 15.4) * mm, "end": v(-5.96, 15.06) * mm});
            skLineSegment(sketch, "E408", {"start": v(-5.96, 15.06) * mm, "end": v(-6.9, 14.66) * mm});
            skLineSegment(sketch, "E409", {"start": v(-6.9, 14.66) * mm, "end": v(-7.8, 14.2) * mm});
            skLineSegment(sketch, "E410", {"start": v(-7.8, 14.2) * mm, "end": v(-8.68, 13.68) * mm});
            skLineSegment(sketch, "E411", {"start": v(-8.68, 13.68) * mm, "end": v(-9.52, 13.1) * mm});
            skLineSegment(sketch, "E412", {"start": v(-9.52, 13.1) * mm, "end": v(-10.32, 12.48) * mm});
            skLineSegment(sketch, "E413", {"start": v(-10.32, 12.48) * mm, "end": v(-11.09, 11.8) * mm});
            skLineSegment(sketch, "E414", {"start": v(-11.09, 11.8) * mm, "end": v(-11.8, 11.09) * mm});
            skLineSegment(sketch, "E415", {"start": v(-11.8, 11.09) * mm, "end": v(-12.48, 10.32) * mm});
            skLineSegment(sketch, "E416", {"start": v(-12.48, 10.32) * mm, "end": v(-13.1, 9.52) * mm});
            skLineSegment(sketch, "E417", {"start": v(-13.1, 9.52) * mm, "end": v(-13.68, 8.68) * mm});
            skLineSegment(sketch, "E418", {"start": v(-13.68, 8.68) * mm, "end": v(-14.2, 7.8) * mm});
            skLineSegment(sketch, "E419", {"start": v(-14.2, 7.8) * mm, "end": v(-14.66, 6.9) * mm});
            skLineSegment(sketch, "E420", {"start": v(-14.66, 6.9) * mm, "end": v(-15.06, 5.96) * mm});
            skLineSegment(sketch, "E421", {"start": v(-15.06, 5.96) * mm, "end": v(-15.4, 5) * mm});
            skLineSegment(sketch, "E422", {"start": v(-15.4, 5) * mm, "end": v(-15.69, 4.03) * mm});
            skLineSegment(sketch, "E423", {"start": v(-15.69, 4.03) * mm, "end": v(-15.91, 3.04) * mm});
            skLineSegment(sketch, "E424", {"start": v(-15.91, 3.04) * mm, "end": v(-16.07, 2.03) * mm});
            skLineSegment(sketch, "E425", {"start": v(-16.07, 2.03) * mm, "end": v(-16.16, 1.09) * mm});
            skLineSegment(sketch, "E426", {"start": v(-16.16, 1.09) * mm, "end": v(-16.04, 1.14) * mm});
            skLineSegment(sketch, "E427", {"start": v(16.17, 1.02) * mm, "end": v(16.07, 2.03) * mm});
            skLineSegment(sketch, "E428", {"start": v(16.07, 2.03) * mm, "end": v(15.91, 3.04) * mm});
            skLineSegment(sketch, "E429", {"start": v(15.91, 3.04) * mm, "end": v(15.69, 4.03) * mm});
            skLineSegment(sketch, "E430", {"start": v(15.69, 4.03) * mm, "end": v(15.4, 5) * mm});
            skLineSegment(sketch, "E431", {"start": v(15.4, 5) * mm, "end": v(15.06, 5.96) * mm});
            skLineSegment(sketch, "E432", {"start": v(15.06, 5.96) * mm, "end": v(14.66, 6.9) * mm});
            skLineSegment(sketch, "E433", {"start": v(14.66, 6.9) * mm, "end": v(14.2, 7.8) * mm});
            skLineSegment(sketch, "E434", {"start": v(14.2, 7.8) * mm, "end": v(13.68, 8.68) * mm});
            skLineSegment(sketch, "E435", {"start": v(13.68, 8.68) * mm, "end": v(13.1, 9.52) * mm});
            skLineSegment(sketch, "E436", {"start": v(13.1, 9.52) * mm, "end": v(12.48, 10.32) * mm});
            skLineSegment(sketch, "E437", {"start": v(12.48, 10.32) * mm, "end": v(11.8, 11.09) * mm});
            skLineSegment(sketch, "E438", {"start": v(11.8, 11.09) * mm, "end": v(11.09, 11.8) * mm});
            skLineSegment(sketch, "E439", {"start": v(11.09, 11.8) * mm, "end": v(10.32, 12.48) * mm});
            skLineSegment(sketch, "E440", {"start": v(10.32, 12.48) * mm, "end": v(9.52, 13.1) * mm});
            skLineSegment(sketch, "E441", {"start": v(9.52, 13.1) * mm, "end": v(8.68, 13.68) * mm});
            skLineSegment(sketch, "E442", {"start": v(8.68, 13.68) * mm, "end": v(7.8, 14.2) * mm});
            skLineSegment(sketch, "E443", {"start": v(7.8, 14.2) * mm, "end": v(6.9, 14.66) * mm});
            skLineSegment(sketch, "E444", {"start": v(6.9, 14.66) * mm, "end": v(5.96, 15.06) * mm});
            skLineSegment(sketch, "E445", {"start": v(5.96, 15.06) * mm, "end": v(5, 15.4) * mm});
            skLineSegment(sketch, "E446", {"start": v(5, 15.4) * mm, "end": v(4.03, 15.69) * mm});
            skLineSegment(sketch, "E447", {"start": v(4.03, 15.69) * mm, "end": v(3.04, 15.91) * mm});
            skLineSegment(sketch, "E448", {"start": v(3.04, 15.91) * mm, "end": v(2.03, 16.07) * mm});
            skLineSegment(sketch, "E449", {"start": v(2.03, 16.07) * mm, "end": v(1.09, 16.16) * mm});
            skLineSegment(sketch, "E450", {"start": v(1.09, 16.16) * mm, "end": v(1.14, 16.04) * mm});
            skLineSegment(sketch, "E451", {"start": v(1.14, 16.04) * mm, "end": v(1.23, 15.83) * mm});
            skLineSegment(sketch, "E452", {"start": v(1.23, 15.83) * mm, "end": v(1.32, 15.61) * mm});
            skLineSegment(sketch, "E453", {"start": v(1.32, 15.61) * mm, "end": v(1.4, 15.4) * mm});
            skLineSegment(sketch, "E454", {"start": v(1.4, 15.4) * mm, "end": v(1.48, 15.19) * mm});
            skLineSegment(sketch, "E455", {"start": v(1.48, 15.19) * mm, "end": v(1.56, 14.97) * mm});
            skLineSegment(sketch, "E456", {"start": v(1.56, 14.97) * mm, "end": v(1.63, 14.76) * mm});
            skLineSegment(sketch, "E457", {"start": v(1.63, 14.76) * mm, "end": v(1.7, 14.54) * mm});
            skLineSegment(sketch, "E458", {"start": v(1.7, 14.54) * mm, "end": v(1.77, 14.33) * mm});
            skLineSegment(sketch, "E459", {"start": v(1.77, 14.33) * mm, "end": v(1.84, 14.11) * mm});
            skLineSegment(sketch, "E460", {"start": v(1.84, 14.11) * mm, "end": v(1.9, 13.9) * mm});
            skLineSegment(sketch, "E461", {"start": v(1.9, 13.9) * mm, "end": v(1.96, 13.68) * mm});
            skLineSegment(sketch, "E462", {"start": v(1.96, 13.68) * mm, "end": v(2.01, 13.47) * mm});
            skLineSegment(sketch, "E463", {"start": v(2.01, 13.47) * mm, "end": v(2.07, 13.25) * mm});
            skLineSegment(sketch, "E464", {"start": v(2.07, 13.25) * mm, "end": v(2.12, 13.04) * mm});
            skLineSegment(sketch, "E465", {"start": v(2.12, 13.04) * mm, "end": v(2.17, 12.82) * mm});
            skLineSegment(sketch, "E466", {"start": v(2.17, 12.82) * mm, "end": v(2.21, 12.6) * mm});
            skLineSegment(sketch, "E467", {"start": v(2.21, 12.6) * mm, "end": v(2.25, 12.39) * mm});
            skLineSegment(sketch, "E468", {"start": v(2.25, 12.39) * mm, "end": v(2.3, 12.17) * mm});
            skLineSegment(sketch, "E469", {"start": v(2.3, 12.17) * mm, "end": v(2.33, 11.96) * mm});
            skLineSegment(sketch, "E470", {"start": v(2.33, 11.96) * mm, "end": v(2.36, 11.74) * mm});
            skLineSegment(sketch, "E471", {"start": v(2.36, 11.74) * mm, "end": v(2.39, 11.52) * mm});
            skLineSegment(sketch, "E472", {"start": v(2.39, 11.52) * mm, "end": v(2.41, 11.3) * mm});
            skLineSegment(sketch, "E473", {"start": v(2.41, 11.3) * mm, "end": v(2.44, 11.09) * mm});
            skLineSegment(sketch, "E474", {"start": v(2.44, 11.09) * mm, "end": v(2.46, 10.87) * mm});
            skLineSegment(sketch, "E475", {"start": v(2.46, 10.87) * mm, "end": v(2.47, 10.65) * mm});
            skLineSegment(sketch, "E476", {"start": v(2.47, 10.65) * mm, "end": v(2.49, 10.43) * mm});
            skLineSegment(sketch, "E477", {"start": v(2.49, 10.43) * mm, "end": v(2.5, 10.22) * mm});
            skLineSegment(sketch, "E478", {"start": v(2.5, 10.22) * mm, "end": v(2.5, 10) * mm});
            skLineSegment(sketch, "E479", {"start": v(2.5, 10) * mm, "end": v(2.51, 9.78) * mm});
            skLineSegment(sketch, "E480", {"start": v(2.51, 9.78) * mm, "end": v(2.51, 9.56) * mm});
            skLineSegment(sketch, "E481", {"start": v(2.51, 9.56) * mm, "end": v(2.51, 9.34) * mm});
            skLineSegment(sketch, "E482", {"start": v(2.51, 9.34) * mm, "end": v(2.5, 9.13) * mm});
            skLineSegment(sketch, "E483", {"start": v(2.5, 9.13) * mm, "end": v(2.5, 8.91) * mm});
            skLineSegment(sketch, "E484", {"start": v(2.5, 8.91) * mm, "end": v(2.49, 8.7) * mm});
            skLineSegment(sketch, "E485", {"start": v(2.49, 8.7) * mm, "end": v(2.47, 8.48) * mm});
            skLineSegment(sketch, "E486", {"start": v(2.47, 8.48) * mm, "end": v(2.46, 8.27) * mm});
            skLineSegment(sketch, "E487", {"start": v(2.46, 8.27) * mm, "end": v(2.44, 8.05) * mm});
            skLineSegment(sketch, "E488", {"start": v(2.44, 8.05) * mm, "end": v(2.42, 7.84) * mm});
            skLineSegment(sketch, "E489", {"start": v(2.42, 7.84) * mm, "end": v(2.4, 7.62) * mm});
            skLineSegment(sketch, "E490", {"start": v(2.4, 7.62) * mm, "end": v(2.36, 7.4) * mm});
            skLineSegment(sketch, "E491", {"start": v(2.36, 7.4) * mm, "end": v(2.33, 7.2) * mm});
            skLineSegment(sketch, "E492", {"start": v(2.33, 7.2) * mm, "end": v(2.3, 6.98) * mm});
            skLineSegment(sketch, "E493", {"start": v(2.3, 6.98) * mm, "end": v(2.26, 6.77) * mm});
            skLineSegment(sketch, "E494", {"start": v(2.26, 6.77) * mm, "end": v(2.22, 6.56) * mm});
            skLineSegment(sketch, "E495", {"start": v(2.22, 6.56) * mm, "end": v(2.18, 6.34) * mm});
            skLineSegment(sketch, "E496", {"start": v(2.18, 6.34) * mm, "end": v(2.13, 6.13) * mm});
            skLineSegment(sketch, "E497", {"start": v(2.13, 6.13) * mm, "end": v(2.08, 5.92) * mm});
            skLineSegment(sketch, "E498", {"start": v(2.08, 5.92) * mm, "end": v(2.03, 5.7) * mm});
            skLineSegment(sketch, "E499", {"start": v(2.03, 5.7) * mm, "end": v(1.97, 5.5) * mm});
            skLineSegment(sketch, "E500", {"start": v(1.97, 5.5) * mm, "end": v(1.92, 5.28) * mm});
            skLineSegment(sketch, "E501", {"start": v(1.92, 5.28) * mm, "end": v(1.85, 5.07) * mm});
            skLineSegment(sketch, "E502", {"start": v(1.85, 5.07) * mm, "end": v(1.8, 4.86) * mm});
            skLineSegment(sketch, "E503", {"start": v(1.8, 4.86) * mm, "end": v(1.72, 4.64) * mm});
            skLineSegment(sketch, "E504", {"start": v(1.72, 4.64) * mm, "end": v(1.66, 4.43) * mm});
            skLineSegment(sketch, "E505", {"start": v(1.66, 4.43) * mm, "end": v(1.58, 4.22) * mm});
            skLineSegment(sketch, "E506", {"start": v(1.58, 4.22) * mm, "end": v(1.5, 4.01) * mm});
            skLineSegment(sketch, "E507", {"start": v(1.5, 4.01) * mm, "end": v(1.43, 3.8) * mm});
            skLineSegment(sketch, "E508", {"start": v(1.43, 3.8) * mm, "end": v(1.35, 3.6) * mm});
            skLineSegment(sketch, "E509", {"start": v(1.35, 3.6) * mm, "end": v(1.26, 3.38) * mm});
            skLineSegment(sketch, "E510", {"start": v(1.26, 3.38) * mm, "end": v(1.18, 3.17) * mm});
            skLineSegment(sketch, "E511", {"start": v(1.18, 3.17) * mm, "end": v(1.12, 3.02) * mm});
            skLineSegment(sketch, "E512", {"start": v(1.12, 3.02) * mm, "end": v(1.19, 3) * mm});
            skLineSegment(sketch, "E513", {"start": v(1.19, 3) * mm, "end": v(1.37, 2.92) * mm});
            skLineSegment(sketch, "E514", {"start": v(1.37, 2.92) * mm, "end": v(1.55, 2.83) * mm});
            skLineSegment(sketch, "E515", {"start": v(1.55, 2.83) * mm, "end": v(1.73, 2.72) * mm});
            skLineSegment(sketch, "E516", {"start": v(1.73, 2.72) * mm, "end": v(1.9, 2.6) * mm});
            skLineSegment(sketch, "E517", {"start": v(1.9, 2.6) * mm, "end": v(2.06, 2.48) * mm});
            skLineSegment(sketch, "E518", {"start": v(2.06, 2.48) * mm, "end": v(2.2, 2.35) * mm});
            skLineSegment(sketch, "E519", {"start": v(2.2, 2.35) * mm, "end": v(2.35, 2.2) * mm});
            skLineSegment(sketch, "E520", {"start": v(2.35, 2.2) * mm, "end": v(2.48, 2.06) * mm});
            skLineSegment(sketch, "E521", {"start": v(2.48, 2.06) * mm, "end": v(2.6, 1.9) * mm});
            skLineSegment(sketch, "E522", {"start": v(2.6, 1.9) * mm, "end": v(2.72, 1.73) * mm});
            skLineSegment(sketch, "E523", {"start": v(2.72, 1.73) * mm, "end": v(2.83, 1.55) * mm});
            skLineSegment(sketch, "E524", {"start": v(2.83, 1.55) * mm, "end": v(2.92, 1.37) * mm});
            skLineSegment(sketch, "E525", {"start": v(2.92, 1.37) * mm, "end": v(3, 1.19) * mm});
            skLineSegment(sketch, "E526", {"start": v(3, 1.19) * mm, "end": v(3.06, 1.02) * mm});
            skLineSegment(sketch, "E527", {"start": v(3.06, 1.02) * mm, "end": v(3.17, 1.07) * mm});
            skLineSegment(sketch, "E528", {"start": v(3.17, 1.07) * mm, "end": v(3.38, 1.17) * mm});
            skLineSegment(sketch, "E529", {"start": v(3.38, 1.17) * mm, "end": v(3.6, 1.27) * mm});
            skLineSegment(sketch, "E530", {"start": v(3.6, 1.27) * mm, "end": v(3.8, 1.36) * mm});
            skLineSegment(sketch, "E531", {"start": v(3.8, 1.36) * mm, "end": v(4.01, 1.45) * mm});
            skLineSegment(sketch, "E532", {"start": v(4.01, 1.45) * mm, "end": v(4.22, 1.54) * mm});
            skLineSegment(sketch, "E533", {"start": v(4.22, 1.54) * mm, "end": v(4.43, 1.63) * mm});
            skLineSegment(sketch, "E534", {"start": v(4.43, 1.63) * mm, "end": v(4.64, 1.7) * mm});
            skLineSegment(sketch, "E535", {"start": v(4.64, 1.7) * mm, "end": v(4.86, 1.78) * mm});
            skLineSegment(sketch, "E536", {"start": v(4.86, 1.78) * mm, "end": v(5.07, 1.86) * mm});
            skLineSegment(sketch, "E537", {"start": v(5.07, 1.86) * mm, "end": v(5.28, 1.93) * mm});
            skLineSegment(sketch, "E538", {"start": v(5.28, 1.93) * mm, "end": v(5.5, 2) * mm});
            skLineSegment(sketch, "E539", {"start": v(5.5, 2) * mm, "end": v(5.7, 2.06) * mm});
            skLineSegment(sketch, "E540", {"start": v(5.7, 2.06) * mm, "end": v(5.92, 2.12) * mm});
            skLineSegment(sketch, "E541", {"start": v(5.92, 2.12) * mm, "end": v(6.13, 2.18) * mm});
            skLineSegment(sketch, "E542", {"start": v(6.13, 2.18) * mm, "end": v(6.34, 2.23) * mm});
            skLineSegment(sketch, "E543", {"start": v(6.34, 2.23) * mm, "end": v(6.56, 2.28) * mm});
            skLineSegment(sketch, "E544", {"start": v(6.56, 2.28) * mm, "end": v(6.77, 2.33) * mm});
            skLineSegment(sketch, "E545", {"start": v(6.77, 2.33) * mm, "end": v(6.98, 2.37) * mm});
            skLineSegment(sketch, "E546", {"start": v(6.98, 2.37) * mm, "end": v(7.2, 2.41) * mm});
            skLineSegment(sketch, "E547", {"start": v(7.2, 2.41) * mm, "end": v(7.4, 2.45) * mm});
            skLineSegment(sketch, "E548", {"start": v(7.4, 2.45) * mm, "end": v(7.62, 2.48) * mm});
            skLineSegment(sketch, "E549", {"start": v(7.62, 2.48) * mm, "end": v(7.84, 2.51) * mm});
            skLineSegment(sketch, "E550", {"start": v(7.84, 2.51) * mm, "end": v(8.05, 2.54) * mm});
            skLineSegment(sketch, "E551", {"start": v(8.05, 2.54) * mm, "end": v(8.27, 2.56) * mm});
            skLineSegment(sketch, "E552", {"start": v(8.27, 2.56) * mm, "end": v(8.48, 2.58) * mm});
            skLineSegment(sketch, "E553", {"start": v(8.48, 2.58) * mm, "end": v(8.7, 2.6) * mm});
            skLineSegment(sketch, "E554", {"start": v(8.7, 2.6) * mm, "end": v(8.91, 2.6) * mm});
            skLineSegment(sketch, "E555", {"start": v(8.91, 2.6) * mm, "end": v(9.13, 2.62) * mm});
            skLineSegment(sketch, "E556", {"start": v(9.13, 2.62) * mm, "end": v(9.34, 2.62) * mm});
            skLineSegment(sketch, "E557", {"start": v(9.34, 2.62) * mm, "end": v(9.56, 2.62) * mm});
            skLineSegment(sketch, "E558", {"start": v(9.56, 2.62) * mm, "end": v(9.78, 2.62) * mm});
            skLineSegment(sketch, "E559", {"start": v(9.78, 2.62) * mm, "end": v(10, 2.62) * mm});
            skLineSegment(sketch, "E560", {"start": v(10, 2.62) * mm, "end": v(10.22, 2.6) * mm});
            skLineSegment(sketch, "E561", {"start": v(10.22, 2.6) * mm, "end": v(10.43, 2.6) * mm});
            skLineSegment(sketch, "E562", {"start": v(10.43, 2.6) * mm, "end": v(10.65, 2.58) * mm});
            skLineSegment(sketch, "E563", {"start": v(10.65, 2.58) * mm, "end": v(10.87, 2.56) * mm});
            skLineSegment(sketch, "E564", {"start": v(10.87, 2.56) * mm, "end": v(11.09, 2.54) * mm});
            skLineSegment(sketch, "E565", {"start": v(11.09, 2.54) * mm, "end": v(11.3, 2.5) * mm});
            skLineSegment(sketch, "E566", {"start": v(11.3, 2.5) * mm, "end": v(11.52, 2.48) * mm});
            skLineSegment(sketch, "E567", {"start": v(11.52, 2.48) * mm, "end": v(11.74, 2.44) * mm});
            skLineSegment(sketch, "E568", {"start": v(11.74, 2.44) * mm, "end": v(11.96, 2.4) * mm});
            skLineSegment(sketch, "E569", {"start": v(11.96, 2.4) * mm, "end": v(12.17, 2.37) * mm});
            skLineSegment(sketch, "E570", {"start": v(12.17, 2.37) * mm, "end": v(12.39, 2.32) * mm});
            skLineSegment(sketch, "E571", {"start": v(12.39, 2.32) * mm, "end": v(12.6, 2.27) * mm});
            skLineSegment(sketch, "E572", {"start": v(12.6, 2.27) * mm, "end": v(12.82, 2.22) * mm});
            skLineSegment(sketch, "E573", {"start": v(12.82, 2.22) * mm, "end": v(13.04, 2.17) * mm});
            skLineSegment(sketch, "E574", {"start": v(13.04, 2.17) * mm, "end": v(13.25, 2.1) * mm});
            skLineSegment(sketch, "E575", {"start": v(13.25, 2.1) * mm, "end": v(13.47, 2.04) * mm});
            skLineSegment(sketch, "E576", {"start": v(13.47, 2.04) * mm, "end": v(13.68, 1.98) * mm});
            skLineSegment(sketch, "E577", {"start": v(13.68, 1.98) * mm, "end": v(13.9, 1.9) * mm});
            skLineSegment(sketch, "E578", {"start": v(13.9, 1.9) * mm, "end": v(14.11, 1.84) * mm});
            skLineSegment(sketch, "E579", {"start": v(14.11, 1.84) * mm, "end": v(14.33, 1.76) * mm});
            skLineSegment(sketch, "E580", {"start": v(14.33, 1.76) * mm, "end": v(14.54, 1.68) * mm});
            skLineSegment(sketch, "E581", {"start": v(14.54, 1.68) * mm, "end": v(14.76, 1.6) * mm});
            skLineSegment(sketch, "E582", {"start": v(14.76, 1.6) * mm, "end": v(14.97, 1.51) * mm});
            skLineSegment(sketch, "E583", {"start": v(14.97, 1.51) * mm, "end": v(15.19, 1.42) * mm});
            skLineSegment(sketch, "E584", {"start": v(15.19, 1.42) * mm, "end": v(15.4, 1.33) * mm});
            skLineSegment(sketch, "E585", {"start": v(15.4, 1.33) * mm, "end": v(15.61, 1.23) * mm});
            skLineSegment(sketch, "E586", {"start": v(15.61, 1.23) * mm, "end": v(15.83, 1.13) * mm});
            skLineSegment(sketch, "E587", {"start": v(15.83, 1.13) * mm, "end": v(16.04, 1.03) * mm});
            skLineSegment(sketch, "E588", {"start": v(16.04, 1.03) * mm, "end": v(16.17, 0.96) * mm});
            skLineSegment(sketch, "E589", {"start": v(16.17, 0.96) * mm, "end": v(16.17, 1.02) * mm});
            skLineSegment(sketch, "E590", {"start": v(0.35, 6.2) * mm, "end": v(0.4, 6.31) * mm});
            skLineSegment(sketch, "E591", {"start": v(0.4, 6.31) * mm, "end": v(0.45, 6.42) * mm});
            skLineSegment(sketch, "E592", {"start": v(0.45, 6.42) * mm, "end": v(0.5, 6.54) * mm});
            skLineSegment(sketch, "E593", {"start": v(0.5, 6.54) * mm, "end": v(0.54, 6.65) * mm});
            skLineSegment(sketch, "E594", {"start": v(0.54, 6.65) * mm, "end": v(0.58, 6.76) * mm});
            skLineSegment(sketch, "E595", {"start": v(0.58, 6.76) * mm, "end": v(0.62, 6.87) * mm});
            skLineSegment(sketch, "E596", {"start": v(0.62, 6.87) * mm, "end": v(0.66, 6.99) * mm});
            skLineSegment(sketch, "E597", {"start": v(0.66, 6.99) * mm, "end": v(0.7, 7.1) * mm});
            skLineSegment(sketch, "E598", {"start": v(0.7, 7.1) * mm, "end": v(0.74, 7.21) * mm});
            skLineSegment(sketch, "E599", {"start": v(0.74, 7.21) * mm, "end": v(0.77, 7.33) * mm});
            skLineSegment(sketch, "E600", {"start": v(0.77, 7.33) * mm, "end": v(0.8, 7.44) * mm});
            skLineSegment(sketch, "E601", {"start": v(0.8, 7.44) * mm, "end": v(0.84, 7.55) * mm});
            skLineSegment(sketch, "E602", {"start": v(0.84, 7.55) * mm, "end": v(0.87, 7.66) * mm});
            skLineSegment(sketch, "E603", {"start": v(0.87, 7.66) * mm, "end": v(0.9, 7.78) * mm});
            skLineSegment(sketch, "E604", {"start": v(0.9, 7.78) * mm, "end": v(0.92, 7.9) * mm});
            skLineSegment(sketch, "E605", {"start": v(0.92, 7.9) * mm, "end": v(0.95, 8) * mm});
            skLineSegment(sketch, "E606", {"start": v(0.95, 8) * mm, "end": v(0.97, 8.12) * mm});
            skLineSegment(sketch, "E607", {"start": v(0.97, 8.12) * mm, "end": v(1, 8.23) * mm});
            skLineSegment(sketch, "E608", {"start": v(1, 8.23) * mm, "end": v(1.01, 8.34) * mm});
            skLineSegment(sketch, "E609", {"start": v(1.01, 8.34) * mm, "end": v(1.03, 8.46) * mm});
            skLineSegment(sketch, "E610", {"start": v(1.03, 8.46) * mm, "end": v(1.04, 8.57) * mm});
            skLineSegment(sketch, "E611", {"start": v(1.04, 8.57) * mm, "end": v(1.06, 8.69) * mm});
            skLineSegment(sketch, "E612", {"start": v(1.06, 8.69) * mm, "end": v(1.07, 8.8) * mm});
            skLineSegment(sketch, "E613", {"start": v(1.07, 8.8) * mm, "end": v(1.08, 8.91) * mm});
            skLineSegment(sketch, "E614", {"start": v(1.08, 8.91) * mm, "end": v(1.1, 9.03) * mm});
            skLineSegment(sketch, "E615", {"start": v(1.1, 9.03) * mm, "end": v(1.1, 9.14) * mm});
            skLineSegment(sketch, "E616", {"start": v(1.1, 9.14) * mm, "end": v(1.1, 9.26) * mm});
            skLineSegment(sketch, "E617", {"start": v(1.1, 9.26) * mm, "end": v(1.11, 9.37) * mm});
            skLineSegment(sketch, "E618", {"start": v(1.11, 9.37) * mm, "end": v(1.11, 9.48) * mm});
            skLineSegment(sketch, "E619", {"start": v(1.11, 9.48) * mm, "end": v(1.11, 9.6) * mm});
            skLineSegment(sketch, "E620", {"start": v(1.11, 9.6) * mm, "end": v(1.11, 9.71) * mm});
            skLineSegment(sketch, "E621", {"start": v(1.11, 9.71) * mm, "end": v(1.11, 9.83) * mm});
            skLineSegment(sketch, "E622", {"start": v(1.11, 9.83) * mm, "end": v(1.1, 9.95) * mm});
            skLineSegment(sketch, "E623", {"start": v(1.1, 9.95) * mm, "end": v(1.1, 10.06) * mm});
            skLineSegment(sketch, "E624", {"start": v(1.1, 10.06) * mm, "end": v(1.1, 10.18) * mm});
            skLineSegment(sketch, "E625", {"start": v(1.1, 10.18) * mm, "end": v(1.08, 10.3) * mm});
            skLineSegment(sketch, "E626", {"start": v(1.08, 10.3) * mm, "end": v(1.07, 10.4) * mm});
            skLineSegment(sketch, "E627", {"start": v(1.07, 10.4) * mm, "end": v(1.06, 10.52) * mm});
            skLineSegment(sketch, "E628", {"start": v(1.06, 10.52) * mm, "end": v(1.04, 10.64) * mm});
            skLineSegment(sketch, "E629", {"start": v(1.04, 10.64) * mm, "end": v(1.03, 10.75) * mm});
            skLineSegment(sketch, "E630", {"start": v(1.03, 10.75) * mm, "end": v(1, 10.87) * mm});
            skLineSegment(sketch, "E631", {"start": v(1, 10.87) * mm, "end": v(0.99, 10.99) * mm});
            skLineSegment(sketch, "E632", {"start": v(0.99, 10.99) * mm, "end": v(0.96, 11.1) * mm});
            skLineSegment(sketch, "E633", {"start": v(0.96, 11.1) * mm, "end": v(0.94, 11.22) * mm});
            skLineSegment(sketch, "E634", {"start": v(0.94, 11.22) * mm, "end": v(0.92, 11.33) * mm});
            skLineSegment(sketch, "E635", {"start": v(0.92, 11.33) * mm, "end": v(0.89, 11.44) * mm});
            skLineSegment(sketch, "E636", {"start": v(0.89, 11.44) * mm, "end": v(0.86, 11.56) * mm});
            skLineSegment(sketch, "E637", {"start": v(0.86, 11.56) * mm, "end": v(0.83, 11.67) * mm});
            skLineSegment(sketch, "E638", {"start": v(0.83, 11.67) * mm, "end": v(0.8, 11.79) * mm});
            skLineSegment(sketch, "E639", {"start": v(0.8, 11.79) * mm, "end": v(0.76, 11.9) * mm});
            skLineSegment(sketch, "E640", {"start": v(0.76, 11.9) * mm, "end": v(0.73, 12.02) * mm});
            skLineSegment(sketch, "E641", {"start": v(0.73, 12.02) * mm, "end": v(0.69, 12.13) * mm});
            skLineSegment(sketch, "E642", {"start": v(0.69, 12.13) * mm, "end": v(0.65, 12.25) * mm});
            skLineSegment(sketch, "E643", {"start": v(0.65, 12.25) * mm, "end": v(0.6, 12.36) * mm});
            skLineSegment(sketch, "E644", {"start": v(0.6, 12.36) * mm, "end": v(0.57, 12.47) * mm});
            skLineSegment(sketch, "E645", {"start": v(0.57, 12.47) * mm, "end": v(0.52, 12.59) * mm});
            skLineSegment(sketch, "E646", {"start": v(0.52, 12.59) * mm, "end": v(0.48, 12.7) * mm});
            skLineSegment(sketch, "E647", {"start": v(0.48, 12.7) * mm, "end": v(0.43, 12.82) * mm});
            skLineSegment(sketch, "E648", {"start": v(0.43, 12.82) * mm, "end": v(0.38, 12.93) * mm});
            skLineSegment(sketch, "E649", {"start": v(0.38, 12.93) * mm, "end": v(0.33, 13.04) * mm});
            skLineSegment(sketch, "E650", {"start": v(0.33, 13.04) * mm, "end": v(0.32, 13.06) * mm});
            skLineSegment(sketch, "E651", {"start": v(0.32, 13.06) * mm, "end": v(-0.23, 13.06) * mm});
            skLineSegment(sketch, "E652", {"start": v(-0.23, 13.06) * mm, "end": v(-0.25, 13.03) * mm});
            skLineSegment(sketch, "E653", {"start": v(-0.25, 13.03) * mm, "end": v(-0.31, 12.91) * mm});
            skLineSegment(sketch, "E654", {"start": v(-0.31, 12.91) * mm, "end": v(-0.37, 12.8) * mm});
            skLineSegment(sketch, "E655", {"start": v(-0.37, 12.8) * mm, "end": v(-0.42, 12.68) * mm});
            skLineSegment(sketch, "E656", {"start": v(-0.42, 12.68) * mm, "end": v(-0.48, 12.57) * mm});
            skLineSegment(sketch, "E657", {"start": v(-0.48, 12.57) * mm, "end": v(-0.53, 12.46) * mm});
            skLineSegment(sketch, "E658", {"start": v(-0.53, 12.46) * mm, "end": v(-0.58, 12.34) * mm});
            skLineSegment(sketch, "E659", {"start": v(-0.58, 12.34) * mm, "end": v(-0.63, 12.23) * mm});
            skLineSegment(sketch, "E660", {"start": v(-0.63, 12.23) * mm, "end": v(-0.67, 12.12) * mm});
            skLineSegment(sketch, "E661", {"start": v(-0.67, 12.12) * mm, "end": v(-0.71, 12) * mm});
            skLineSegment(sketch, "E662", {"start": v(-0.71, 12) * mm, "end": v(-0.76, 11.89) * mm});
            skLineSegment(sketch, "E663", {"start": v(-0.76, 11.89) * mm, "end": v(-0.8, 11.77) * mm});
            skLineSegment(sketch, "E664", {"start": v(-0.8, 11.77) * mm, "end": v(-0.83, 11.66) * mm});
            skLineSegment(sketch, "E665", {"start": v(-0.83, 11.66) * mm, "end": v(-0.87, 11.55) * mm});
            skLineSegment(sketch, "E666", {"start": v(-0.87, 11.55) * mm, "end": v(-0.9, 11.43) * mm});
            skLineSegment(sketch, "E667", {"start": v(-0.9, 11.43) * mm, "end": v(-0.93, 11.32) * mm});
            skLineSegment(sketch, "E668", {"start": v(-0.93, 11.32) * mm, "end": v(-0.96, 11.2) * mm});
            skLineSegment(sketch, "E669", {"start": v(-0.96, 11.2) * mm, "end": v(-1, 11.09) * mm});
            skLineSegment(sketch, "E670", {"start": v(-1, 11.09) * mm, "end": v(-1.02, 10.98) * mm});
            skLineSegment(sketch, "E671", {"start": v(-1.02, 10.98) * mm, "end": v(-1.04, 10.86) * mm});
            skLineSegment(sketch, "E672", {"start": v(-1.04, 10.86) * mm, "end": v(-1.06, 10.75) * mm});
            skLineSegment(sketch, "E673", {"start": v(-1.06, 10.75) * mm, "end": v(-1.08, 10.63) * mm});
            skLineSegment(sketch, "E674", {"start": v(-1.08, 10.63) * mm, "end": v(-1.1, 10.52) * mm});
            skLineSegment(sketch, "E675", {"start": v(-1.1, 10.52) * mm, "end": v(-1.11, 10.4) * mm});
            skLineSegment(sketch, "E676", {"start": v(-1.11, 10.4) * mm, "end": v(-1.13, 10.29) * mm});
            skLineSegment(sketch, "E677", {"start": v(-1.13, 10.29) * mm, "end": v(-1.14, 10.17) * mm});
            skLineSegment(sketch, "E678", {"start": v(-1.14, 10.17) * mm, "end": v(-1.15, 10.06) * mm});
            skLineSegment(sketch, "E679", {"start": v(-1.15, 10.06) * mm, "end": v(-1.15, 9.94) * mm});
            skLineSegment(sketch, "E680", {"start": v(-1.15, 9.94) * mm, "end": v(-1.16, 9.83) * mm});
            skLineSegment(sketch, "E681", {"start": v(-1.16, 9.83) * mm, "end": v(-1.16, 9.71) * mm});
            skLineSegment(sketch, "E682", {"start": v(-1.16, 9.71) * mm, "end": v(-1.16, 9.6) * mm});
            skLineSegment(sketch, "E683", {"start": v(-1.16, 9.6) * mm, "end": v(-1.16, 9.48) * mm});
            skLineSegment(sketch, "E684", {"start": v(-1.16, 9.48) * mm, "end": v(-1.16, 9.37) * mm});
            skLineSegment(sketch, "E685", {"start": v(-1.16, 9.37) * mm, "end": v(-1.15, 9.26) * mm});
            skLineSegment(sketch, "E686", {"start": v(-1.15, 9.26) * mm, "end": v(-1.15, 9.14) * mm});
            skLineSegment(sketch, "E687", {"start": v(-1.15, 9.14) * mm, "end": v(-1.14, 9.03) * mm});
            skLineSegment(sketch, "E688", {"start": v(-1.14, 9.03) * mm, "end": v(-1.13, 8.92) * mm});
            skLineSegment(sketch, "E689", {"start": v(-1.13, 8.92) * mm, "end": v(-1.11, 8.8) * mm});
            skLineSegment(sketch, "E690", {"start": v(-1.11, 8.8) * mm, "end": v(-1.1, 8.7) * mm});
            skLineSegment(sketch, "E691", {"start": v(-1.1, 8.7) * mm, "end": v(-1.08, 8.58) * mm});
            skLineSegment(sketch, "E692", {"start": v(-1.08, 8.58) * mm, "end": v(-1.06, 8.47) * mm});
            skLineSegment(sketch, "E693", {"start": v(-1.06, 8.47) * mm, "end": v(-1.04, 8.35) * mm});
            skLineSegment(sketch, "E694", {"start": v(-1.04, 8.35) * mm, "end": v(-1.02, 8.24) * mm});
            skLineSegment(sketch, "E695", {"start": v(-1.02, 8.24) * mm, "end": v(-1, 8.13) * mm});
            skLineSegment(sketch, "E696", {"start": v(-1, 8.13) * mm, "end": v(-0.97, 8.02) * mm});
            skLineSegment(sketch, "E697", {"start": v(-0.97, 8.02) * mm, "end": v(-0.94, 7.9) * mm});
            skLineSegment(sketch, "E698", {"start": v(-0.94, 7.9) * mm, "end": v(-0.9, 7.8) * mm});
            skLineSegment(sketch, "E699", {"start": v(-0.9, 7.8) * mm, "end": v(-0.88, 7.68) * mm});
            skLineSegment(sketch, "E700", {"start": v(-0.88, 7.68) * mm, "end": v(-0.84, 7.57) * mm});
            skLineSegment(sketch, "E701", {"start": v(-0.84, 7.57) * mm, "end": v(-0.8, 7.45) * mm});
            skLineSegment(sketch, "E702", {"start": v(-0.8, 7.45) * mm, "end": v(-0.77, 7.34) * mm});
            skLineSegment(sketch, "E703", {"start": v(-0.77, 7.34) * mm, "end": v(-0.73, 7.23) * mm});
            skLineSegment(sketch, "E704", {"start": v(-0.73, 7.23) * mm, "end": v(-0.69, 7.12) * mm});
            skLineSegment(sketch, "E705", {"start": v(-0.69, 7.12) * mm, "end": v(-0.64, 7) * mm});
            skLineSegment(sketch, "E706", {"start": v(-0.64, 7) * mm, "end": v(-0.6, 6.9) * mm});
            skLineSegment(sketch, "E707", {"start": v(-0.6, 6.9) * mm, "end": v(-0.55, 6.78) * mm});
            skLineSegment(sketch, "E708", {"start": v(-0.55, 6.78) * mm, "end": v(-0.5, 6.67) * mm});
            skLineSegment(sketch, "E709", {"start": v(-0.5, 6.67) * mm, "end": v(-0.44, 6.56) * mm});
            skLineSegment(sketch, "E710", {"start": v(-0.44, 6.56) * mm, "end": v(-0.4, 6.44) * mm});
            skLineSegment(sketch, "E711", {"start": v(-0.4, 6.44) * mm, "end": v(-0.33, 6.33) * mm});
            skLineSegment(sketch, "E712", {"start": v(-0.33, 6.33) * mm, "end": v(-0.28, 6.22) * mm});
            skLineSegment(sketch, "E713", {"start": v(-0.28, 6.22) * mm, "end": v(-0.26, 6.2) * mm});
            skLineSegment(sketch, "E714", {"start": v(-0.26, 6.2) * mm, "end": v(0.34, 6.2) * mm});
            skLineSegment(sketch, "E715", {"start": v(0.34, 6.2) * mm, "end": v(0.35, 6.2) * mm});
            skLineSegment(sketch, "E716", {"start": v(9.71, -1.11) * mm, "end": v(9.83, -1.11) * mm});
            skLineSegment(sketch, "E717", {"start": v(9.83, -1.11) * mm, "end": v(9.95, -1.1) * mm});
            skLineSegment(sketch, "E718", {"start": v(9.95, -1.1) * mm, "end": v(10.06, -1.1) * mm});
            skLineSegment(sketch, "E719", {"start": v(10.06, -1.1) * mm, "end": v(10.18, -1.1) * mm});
            skLineSegment(sketch, "E720", {"start": v(10.18, -1.1) * mm, "end": v(10.3, -1.08) * mm});
            skLineSegment(sketch, "E721", {"start": v(10.3, -1.08) * mm, "end": v(10.4, -1.07) * mm});
            skLineSegment(sketch, "E722", {"start": v(10.4, -1.07) * mm, "end": v(10.52, -1.06) * mm});
            skLineSegment(sketch, "E723", {"start": v(10.52, -1.06) * mm, "end": v(10.64, -1.04) * mm});
            skLineSegment(sketch, "E724", {"start": v(10.64, -1.04) * mm, "end": v(10.75, -1.03) * mm});
            skLineSegment(sketch, "E725", {"start": v(10.75, -1.03) * mm, "end": v(10.87, -1) * mm});
            skLineSegment(sketch, "E726", {"start": v(10.87, -1) * mm, "end": v(10.99, -0.99) * mm});
            skLineSegment(sketch, "E727", {"start": v(10.99, -0.99) * mm, "end": v(11.1, -0.96) * mm});
            skLineSegment(sketch, "E728", {"start": v(11.1, -0.96) * mm, "end": v(11.22, -0.94) * mm});
            skLineSegment(sketch, "E729", {"start": v(11.22, -0.94) * mm, "end": v(11.33, -0.92) * mm});
            skLineSegment(sketch, "E730", {"start": v(11.33, -0.92) * mm, "end": v(11.44, -0.89) * mm});
            skLineSegment(sketch, "E731", {"start": v(11.44, -0.89) * mm, "end": v(11.56, -0.86) * mm});
            skLineSegment(sketch, "E732", {"start": v(11.56, -0.86) * mm, "end": v(11.67, -0.83) * mm});
            skLineSegment(sketch, "E733", {"start": v(11.67, -0.83) * mm, "end": v(11.79, -0.8) * mm});
            skLineSegment(sketch, "E734", {"start": v(11.79, -0.8) * mm, "end": v(11.9, -0.76) * mm});
            skLineSegment(sketch, "E735", {"start": v(11.9, -0.76) * mm, "end": v(12.02, -0.73) * mm});
            skLineSegment(sketch, "E736", {"start": v(12.02, -0.73) * mm, "end": v(12.13, -0.69) * mm});
            skLineSegment(sketch, "E737", {"start": v(12.13, -0.69) * mm, "end": v(12.25, -0.65) * mm});
            skLineSegment(sketch, "E738", {"start": v(12.25, -0.65) * mm, "end": v(12.36, -0.6) * mm});
            skLineSegment(sketch, "E739", {"start": v(12.36, -0.6) * mm, "end": v(12.47, -0.57) * mm});
            skLineSegment(sketch, "E740", {"start": v(12.47, -0.57) * mm, "end": v(12.59, -0.52) * mm});
            skLineSegment(sketch, "E741", {"start": v(12.59, -0.52) * mm, "end": v(12.7, -0.48) * mm});
            skLineSegment(sketch, "E742", {"start": v(12.7, -0.48) * mm, "end": v(12.82, -0.43) * mm});
            skLineSegment(sketch, "E743", {"start": v(12.82, -0.43) * mm, "end": v(12.93, -0.38) * mm});
            skLineSegment(sketch, "E744", {"start": v(12.93, -0.38) * mm, "end": v(13.04, -0.33) * mm});
            skLineSegment(sketch, "E745", {"start": v(13.04, -0.33) * mm, "end": v(13.06, -0.32) * mm});
            skLineSegment(sketch, "E746", {"start": v(13.06, -0.32) * mm, "end": v(13.06, 0.23) * mm});
            skLineSegment(sketch, "E747", {"start": v(13.06, 0.23) * mm, "end": v(13.03, 0.25) * mm});
            skLineSegment(sketch, "E748", {"start": v(13.03, 0.25) * mm, "end": v(12.91, 0.31) * mm});
            skLineSegment(sketch, "E749", {"start": v(12.91, 0.31) * mm, "end": v(12.8, 0.37) * mm});
            skLineSegment(sketch, "E750", {"start": v(12.8, 0.37) * mm, "end": v(12.68, 0.42) * mm});
            skLineSegment(sketch, "E751", {"start": v(12.68, 0.42) * mm, "end": v(12.57, 0.48) * mm});
            skLineSegment(sketch, "E752", {"start": v(12.57, 0.48) * mm, "end": v(12.46, 0.53) * mm});
            skLineSegment(sketch, "E753", {"start": v(12.46, 0.53) * mm, "end": v(12.34, 0.58) * mm});
            skLineSegment(sketch, "E754", {"start": v(12.34, 0.58) * mm, "end": v(12.23, 0.63) * mm});
            skLineSegment(sketch, "E755", {"start": v(12.23, 0.63) * mm, "end": v(12.12, 0.67) * mm});
            skLineSegment(sketch, "E756", {"start": v(12.12, 0.67) * mm, "end": v(12, 0.71) * mm});
            skLineSegment(sketch, "E757", {"start": v(12, 0.71) * mm, "end": v(11.89, 0.76) * mm});
            skLineSegment(sketch, "E758", {"start": v(11.89, 0.76) * mm, "end": v(11.77, 0.8) * mm});
            skLineSegment(sketch, "E759", {"start": v(11.77, 0.8) * mm, "end": v(11.66, 0.83) * mm});
            skLineSegment(sketch, "E760", {"start": v(11.66, 0.83) * mm, "end": v(11.55, 0.87) * mm});
            skLineSegment(sketch, "E761", {"start": v(11.55, 0.87) * mm, "end": v(11.43, 0.9) * mm});
            skLineSegment(sketch, "E762", {"start": v(11.43, 0.9) * mm, "end": v(11.32, 0.93) * mm});
            skLineSegment(sketch, "E763", {"start": v(11.32, 0.93) * mm, "end": v(11.2, 0.96) * mm});
            skLineSegment(sketch, "E764", {"start": v(11.2, 0.96) * mm, "end": v(11.09, 1) * mm});
            skLineSegment(sketch, "E765", {"start": v(11.09, 1) * mm, "end": v(10.98, 1.02) * mm});
            skLineSegment(sketch, "E766", {"start": v(10.98, 1.02) * mm, "end": v(10.86, 1.04) * mm});
            skLineSegment(sketch, "E767", {"start": v(10.86, 1.04) * mm, "end": v(10.75, 1.06) * mm});
            skLineSegment(sketch, "E768", {"start": v(10.75, 1.06) * mm, "end": v(10.63, 1.08) * mm});
            skLineSegment(sketch, "E769", {"start": v(10.63, 1.08) * mm, "end": v(10.52, 1.1) * mm});
            skLineSegment(sketch, "E770", {"start": v(10.52, 1.1) * mm, "end": v(10.4, 1.11) * mm});
            skLineSegment(sketch, "E771", {"start": v(10.4, 1.11) * mm, "end": v(10.29, 1.13) * mm});
            skLineSegment(sketch, "E772", {"start": v(10.29, 1.13) * mm, "end": v(10.17, 1.14) * mm});
            skLineSegment(sketch, "E773", {"start": v(10.17, 1.14) * mm, "end": v(10.06, 1.15) * mm});
            skLineSegment(sketch, "E774", {"start": v(10.06, 1.15) * mm, "end": v(9.94, 1.15) * mm});
            skLineSegment(sketch, "E775", {"start": v(9.94, 1.15) * mm, "end": v(9.83, 1.16) * mm});
            skLineSegment(sketch, "E776", {"start": v(9.83, 1.16) * mm, "end": v(9.71, 1.16) * mm});
            skLineSegment(sketch, "E777", {"start": v(9.71, 1.16) * mm, "end": v(9.6, 1.16) * mm});
            skLineSegment(sketch, "E778", {"start": v(9.6, 1.16) * mm, "end": v(9.48, 1.16) * mm});
            skLineSegment(sketch, "E779", {"start": v(9.48, 1.16) * mm, "end": v(9.37, 1.16) * mm});
            skLineSegment(sketch, "E780", {"start": v(9.37, 1.16) * mm, "end": v(9.26, 1.15) * mm});
            skLineSegment(sketch, "E781", {"start": v(9.26, 1.15) * mm, "end": v(9.14, 1.15) * mm});
            skLineSegment(sketch, "E782", {"start": v(9.14, 1.15) * mm, "end": v(9.03, 1.14) * mm});
            skLineSegment(sketch, "E783", {"start": v(9.03, 1.14) * mm, "end": v(8.92, 1.13) * mm});
            skLineSegment(sketch, "E784", {"start": v(8.92, 1.13) * mm, "end": v(8.8, 1.11) * mm});
            skLineSegment(sketch, "E785", {"start": v(8.8, 1.11) * mm, "end": v(8.7, 1.1) * mm});
            skLineSegment(sketch, "E786", {"start": v(8.7, 1.1) * mm, "end": v(8.58, 1.08) * mm});
            skLineSegment(sketch, "E787", {"start": v(8.58, 1.08) * mm, "end": v(8.47, 1.06) * mm});
            skLineSegment(sketch, "E788", {"start": v(8.47, 1.06) * mm, "end": v(8.35, 1.04) * mm});
            skLineSegment(sketch, "E789", {"start": v(8.35, 1.04) * mm, "end": v(8.24, 1.02) * mm});
            skLineSegment(sketch, "E790", {"start": v(8.24, 1.02) * mm, "end": v(8.13, 1) * mm});
            skLineSegment(sketch, "E791", {"start": v(8.13, 1) * mm, "end": v(8.02, 0.97) * mm});
            skLineSegment(sketch, "E792", {"start": v(8.02, 0.97) * mm, "end": v(7.9, 0.94) * mm});
            skLineSegment(sketch, "E793", {"start": v(7.9, 0.94) * mm, "end": v(7.8, 0.9) * mm});
            skLineSegment(sketch, "E794", {"start": v(7.8, 0.9) * mm, "end": v(7.68, 0.88) * mm});
            skLineSegment(sketch, "E795", {"start": v(7.68, 0.88) * mm, "end": v(7.57, 0.84) * mm});
            skLineSegment(sketch, "E796", {"start": v(7.57, 0.84) * mm, "end": v(7.45, 0.8) * mm});
            skLineSegment(sketch, "E797", {"start": v(7.45, 0.8) * mm, "end": v(7.34, 0.77) * mm});
            skLineSegment(sketch, "E798", {"start": v(7.34, 0.77) * mm, "end": v(7.23, 0.73) * mm});
            skLineSegment(sketch, "E799", {"start": v(7.23, 0.73) * mm, "end": v(7.12, 0.69) * mm});
            skLineSegment(sketch, "E800", {"start": v(7.12, 0.69) * mm, "end": v(7, 0.64) * mm});
            skLineSegment(sketch, "E801", {"start": v(7, 0.64) * mm, "end": v(6.9, 0.6) * mm});
            skLineSegment(sketch, "E802", {"start": v(6.9, 0.6) * mm, "end": v(6.78, 0.55) * mm});
            skLineSegment(sketch, "E803", {"start": v(6.78, 0.55) * mm, "end": v(6.67, 0.5) * mm});
            skLineSegment(sketch, "E804", {"start": v(6.67, 0.5) * mm, "end": v(6.56, 0.44) * mm});
            skLineSegment(sketch, "E805", {"start": v(6.56, 0.44) * mm, "end": v(6.44, 0.4) * mm});
            skLineSegment(sketch, "E806", {"start": v(6.44, 0.4) * mm, "end": v(6.33, 0.33) * mm});
            skLineSegment(sketch, "E807", {"start": v(6.33, 0.33) * mm, "end": v(6.22, 0.28) * mm});
            skLineSegment(sketch, "E808", {"start": v(6.22, 0.28) * mm, "end": v(6.2, 0.26) * mm});
            skLineSegment(sketch, "E809", {"start": v(6.2, 0.26) * mm, "end": v(6.2, -0.34) * mm});
            skLineSegment(sketch, "E810", {"start": v(6.2, -0.34) * mm, "end": v(6.2, -0.35) * mm});
            skLineSegment(sketch, "E811", {"start": v(6.2, -0.35) * mm, "end": v(6.31, -0.4) * mm});
            skLineSegment(sketch, "E812", {"start": v(6.31, -0.4) * mm, "end": v(6.42, -0.45) * mm});
            skLineSegment(sketch, "E813", {"start": v(6.42, -0.45) * mm, "end": v(6.54, -0.5) * mm});
            skLineSegment(sketch, "E814", {"start": v(6.54, -0.5) * mm, "end": v(6.65, -0.54) * mm});
            skLineSegment(sketch, "E815", {"start": v(6.65, -0.54) * mm, "end": v(6.76, -0.58) * mm});
            skLineSegment(sketch, "E816", {"start": v(6.76, -0.58) * mm, "end": v(6.87, -0.62) * mm});
            skLineSegment(sketch, "E817", {"start": v(6.87, -0.62) * mm, "end": v(6.99, -0.66) * mm});
            skLineSegment(sketch, "E818", {"start": v(6.99, -0.66) * mm, "end": v(7.1, -0.7) * mm});
            skLineSegment(sketch, "E819", {"start": v(7.1, -0.7) * mm, "end": v(7.21, -0.74) * mm});
            skLineSegment(sketch, "E820", {"start": v(7.21, -0.74) * mm, "end": v(7.33, -0.77) * mm});
            skLineSegment(sketch, "E821", {"start": v(7.33, -0.77) * mm, "end": v(7.44, -0.8) * mm});
            skLineSegment(sketch, "E822", {"start": v(7.44, -0.8) * mm, "end": v(7.55, -0.84) * mm});
            skLineSegment(sketch, "E823", {"start": v(7.55, -0.84) * mm, "end": v(7.66, -0.87) * mm});
            skLineSegment(sketch, "E824", {"start": v(7.66, -0.87) * mm, "end": v(7.78, -0.9) * mm});
            skLineSegment(sketch, "E825", {"start": v(7.78, -0.9) * mm, "end": v(7.9, -0.92) * mm});
            skLineSegment(sketch, "E826", {"start": v(7.9, -0.92) * mm, "end": v(8, -0.95) * mm});
            skLineSegment(sketch, "E827", {"start": v(8, -0.95) * mm, "end": v(8.12, -0.97) * mm});
            skLineSegment(sketch, "E828", {"start": v(8.12, -0.97) * mm, "end": v(8.23, -1) * mm});
            skLineSegment(sketch, "E829", {"start": v(8.23, -1) * mm, "end": v(8.34, -1.01) * mm});
            skLineSegment(sketch, "E830", {"start": v(8.34, -1.01) * mm, "end": v(8.46, -1.03) * mm});
            skLineSegment(sketch, "E831", {"start": v(8.46, -1.03) * mm, "end": v(8.57, -1.04) * mm});
            skLineSegment(sketch, "E832", {"start": v(8.57, -1.04) * mm, "end": v(8.69, -1.06) * mm});
            skLineSegment(sketch, "E833", {"start": v(8.69, -1.06) * mm, "end": v(8.8, -1.07) * mm});
            skLineSegment(sketch, "E834", {"start": v(8.8, -1.07) * mm, "end": v(8.91, -1.08) * mm});
            skLineSegment(sketch, "E835", {"start": v(8.91, -1.08) * mm, "end": v(9.03, -1.1) * mm});
            skLineSegment(sketch, "E836", {"start": v(9.03, -1.1) * mm, "end": v(9.14, -1.1) * mm});
            skLineSegment(sketch, "E837", {"start": v(9.14, -1.1) * mm, "end": v(9.26, -1.1) * mm});
            skLineSegment(sketch, "E838", {"start": v(9.26, -1.1) * mm, "end": v(9.37, -1.11) * mm});
            skLineSegment(sketch, "E839", {"start": v(9.37, -1.11) * mm, "end": v(9.48, -1.11) * mm});
            skLineSegment(sketch, "E840", {"start": v(9.48, -1.11) * mm, "end": v(9.6, -1.11) * mm});
            skLineSegment(sketch, "E841", {"start": v(9.6, -1.11) * mm, "end": v(9.71, -1.11) * mm});
            skLineSegment(sketch, "E842", {"start": v(-9.48, -1.16) * mm, "end": v(-9.37, -1.16) * mm});
            skLineSegment(sketch, "E843", {"start": v(-9.37, -1.16) * mm, "end": v(-9.26, -1.15) * mm});
            skLineSegment(sketch, "E844", {"start": v(-9.26, -1.15) * mm, "end": v(-9.14, -1.15) * mm});
            skLineSegment(sketch, "E845", {"start": v(-9.14, -1.15) * mm, "end": v(-9.03, -1.14) * mm});
            skLineSegment(sketch, "E846", {"start": v(-9.03, -1.14) * mm, "end": v(-8.92, -1.13) * mm});
            skLineSegment(sketch, "E847", {"start": v(-8.92, -1.13) * mm, "end": v(-8.8, -1.11) * mm});
            skLineSegment(sketch, "E848", {"start": v(-8.8, -1.11) * mm, "end": v(-8.7, -1.1) * mm});
            skLineSegment(sketch, "E849", {"start": v(-8.7, -1.1) * mm, "end": v(-8.58, -1.08) * mm});
            skLineSegment(sketch, "E850", {"start": v(-8.58, -1.08) * mm, "end": v(-8.47, -1.06) * mm});
            skLineSegment(sketch, "E851", {"start": v(-8.47, -1.06) * mm, "end": v(-8.35, -1.04) * mm});
            skLineSegment(sketch, "E852", {"start": v(-8.35, -1.04) * mm, "end": v(-8.24, -1.02) * mm});
            skLineSegment(sketch, "E853", {"start": v(-8.24, -1.02) * mm, "end": v(-8.13, -1) * mm});
            skLineSegment(sketch, "E854", {"start": v(-8.13, -1) * mm, "end": v(-8.02, -0.97) * mm});
            skLineSegment(sketch, "E855", {"start": v(-8.02, -0.97) * mm, "end": v(-7.9, -0.94) * mm});
            skLineSegment(sketch, "E856", {"start": v(-7.9, -0.94) * mm, "end": v(-7.8, -0.9) * mm});
            skLineSegment(sketch, "E857", {"start": v(-7.8, -0.9) * mm, "end": v(-7.68, -0.88) * mm});
            skLineSegment(sketch, "E858", {"start": v(-7.68, -0.88) * mm, "end": v(-7.57, -0.84) * mm});
            skLineSegment(sketch, "E859", {"start": v(-7.57, -0.84) * mm, "end": v(-7.45, -0.8) * mm});
            skLineSegment(sketch, "E860", {"start": v(-7.45, -0.8) * mm, "end": v(-7.34, -0.77) * mm});
            skLineSegment(sketch, "E861", {"start": v(-7.34, -0.77) * mm, "end": v(-7.23, -0.73) * mm});
            skLineSegment(sketch, "E862", {"start": v(-7.23, -0.73) * mm, "end": v(-7.12, -0.69) * mm});
            skLineSegment(sketch, "E863", {"start": v(-7.12, -0.69) * mm, "end": v(-7, -0.64) * mm});
            skLineSegment(sketch, "E864", {"start": v(-7, -0.64) * mm, "end": v(-6.9, -0.6) * mm});
            skLineSegment(sketch, "E865", {"start": v(-6.9, -0.6) * mm, "end": v(-6.78, -0.55) * mm});
            skLineSegment(sketch, "E866", {"start": v(-6.78, -0.55) * mm, "end": v(-6.67, -0.5) * mm});
            skLineSegment(sketch, "E867", {"start": v(-6.67, -0.5) * mm, "end": v(-6.56, -0.44) * mm});
            skLineSegment(sketch, "E868", {"start": v(-6.56, -0.44) * mm, "end": v(-6.44, -0.4) * mm});
            skLineSegment(sketch, "E869", {"start": v(-6.44, -0.4) * mm, "end": v(-6.33, -0.33) * mm});
            skLineSegment(sketch, "E870", {"start": v(-6.33, -0.33) * mm, "end": v(-6.22, -0.28) * mm});
            skLineSegment(sketch, "E871", {"start": v(-6.22, -0.28) * mm, "end": v(-6.2, -0.26) * mm});
            skLineSegment(sketch, "E872", {"start": v(-6.2, -0.26) * mm, "end": v(-6.2, 0.34) * mm});
            skLineSegment(sketch, "E873", {"start": v(-6.2, 0.34) * mm, "end": v(-6.2, 0.35) * mm});
            skLineSegment(sketch, "E874", {"start": v(-6.2, 0.35) * mm, "end": v(-6.31, 0.4) * mm});
            skLineSegment(sketch, "E875", {"start": v(-6.31, 0.4) * mm, "end": v(-6.42, 0.45) * mm});
            skLineSegment(sketch, "E876", {"start": v(-6.42, 0.45) * mm, "end": v(-6.54, 0.5) * mm});
            skLineSegment(sketch, "E877", {"start": v(-6.54, 0.5) * mm, "end": v(-6.65, 0.54) * mm});
            skLineSegment(sketch, "E878", {"start": v(-6.65, 0.54) * mm, "end": v(-6.76, 0.58) * mm});
            skLineSegment(sketch, "E879", {"start": v(-6.76, 0.58) * mm, "end": v(-6.87, 0.62) * mm});
            skLineSegment(sketch, "E880", {"start": v(-6.87, 0.62) * mm, "end": v(-6.99, 0.66) * mm});
            skLineSegment(sketch, "E881", {"start": v(-6.99, 0.66) * mm, "end": v(-7.1, 0.7) * mm});
            skLineSegment(sketch, "E882", {"start": v(-7.1, 0.7) * mm, "end": v(-7.21, 0.74) * mm});
            skLineSegment(sketch, "E883", {"start": v(-7.21, 0.74) * mm, "end": v(-7.33, 0.77) * mm});
            skLineSegment(sketch, "E884", {"start": v(-7.33, 0.77) * mm, "end": v(-7.44, 0.8) * mm});
            skLineSegment(sketch, "E885", {"start": v(-7.44, 0.8) * mm, "end": v(-7.55, 0.84) * mm});
            skLineSegment(sketch, "E886", {"start": v(-7.55, 0.84) * mm, "end": v(-7.66, 0.87) * mm});
            skLineSegment(sketch, "E887", {"start": v(-7.66, 0.87) * mm, "end": v(-7.78, 0.9) * mm});
            skLineSegment(sketch, "E888", {"start": v(-7.78, 0.9) * mm, "end": v(-7.9, 0.92) * mm});
            skLineSegment(sketch, "E889", {"start": v(-7.9, 0.92) * mm, "end": v(-8, 0.95) * mm});
            skLineSegment(sketch, "E890", {"start": v(-8, 0.95) * mm, "end": v(-8.12, 0.97) * mm});
            skLineSegment(sketch, "E891", {"start": v(-8.12, 0.97) * mm, "end": v(-8.23, 1) * mm});
            skLineSegment(sketch, "E892", {"start": v(-8.23, 1) * mm, "end": v(-8.34, 1.01) * mm});
            skLineSegment(sketch, "E893", {"start": v(-8.34, 1.01) * mm, "end": v(-8.46, 1.03) * mm});
            skLineSegment(sketch, "E894", {"start": v(-8.46, 1.03) * mm, "end": v(-8.57, 1.04) * mm});
            skLineSegment(sketch, "E895", {"start": v(-8.57, 1.04) * mm, "end": v(-8.69, 1.06) * mm});
            skLineSegment(sketch, "E896", {"start": v(-8.69, 1.06) * mm, "end": v(-8.8, 1.07) * mm});
            skLineSegment(sketch, "E897", {"start": v(-8.8, 1.07) * mm, "end": v(-8.91, 1.08) * mm});
            skLineSegment(sketch, "E898", {"start": v(-8.91, 1.08) * mm, "end": v(-9.03, 1.1) * mm});
            skLineSegment(sketch, "E899", {"start": v(-9.03, 1.1) * mm, "end": v(-9.14, 1.1) * mm});
            skLineSegment(sketch, "E900", {"start": v(-9.14, 1.1) * mm, "end": v(-9.26, 1.1) * mm});
            skLineSegment(sketch, "E901", {"start": v(-9.26, 1.1) * mm, "end": v(-9.37, 1.11) * mm});
            skLineSegment(sketch, "E902", {"start": v(-9.37, 1.11) * mm, "end": v(-9.48, 1.11) * mm});
            skLineSegment(sketch, "E903", {"start": v(-9.48, 1.11) * mm, "end": v(-9.6, 1.11) * mm});
            skLineSegment(sketch, "E904", {"start": v(-9.6, 1.11) * mm, "end": v(-9.71, 1.11) * mm});
            skLineSegment(sketch, "E905", {"start": v(-9.71, 1.11) * mm, "end": v(-9.83, 1.11) * mm});
            skLineSegment(sketch, "E906", {"start": v(-9.83, 1.11) * mm, "end": v(-9.95, 1.1) * mm});
            skLineSegment(sketch, "E907", {"start": v(-9.95, 1.1) * mm, "end": v(-10.06, 1.1) * mm});
            skLineSegment(sketch, "E908", {"start": v(-10.06, 1.1) * mm, "end": v(-10.18, 1.1) * mm});
            skLineSegment(sketch, "E909", {"start": v(-10.18, 1.1) * mm, "end": v(-10.3, 1.08) * mm});
            skLineSegment(sketch, "E910", {"start": v(-10.3, 1.08) * mm, "end": v(-10.4, 1.07) * mm});
            skLineSegment(sketch, "E911", {"start": v(-10.4, 1.07) * mm, "end": v(-10.52, 1.06) * mm});
            skLineSegment(sketch, "E912", {"start": v(-10.52, 1.06) * mm, "end": v(-10.64, 1.04) * mm});
            skLineSegment(sketch, "E913", {"start": v(-10.64, 1.04) * mm, "end": v(-10.75, 1.03) * mm});
            skLineSegment(sketch, "E914", {"start": v(-10.75, 1.03) * mm, "end": v(-10.87, 1) * mm});
            skLineSegment(sketch, "E915", {"start": v(-10.87, 1) * mm, "end": v(-10.99, 0.99) * mm});
            skLineSegment(sketch, "E916", {"start": v(-10.99, 0.99) * mm, "end": v(-11.1, 0.96) * mm});
            skLineSegment(sketch, "E917", {"start": v(-11.1, 0.96) * mm, "end": v(-11.22, 0.94) * mm});
            skLineSegment(sketch, "E918", {"start": v(-11.22, 0.94) * mm, "end": v(-11.33, 0.92) * mm});
            skLineSegment(sketch, "E919", {"start": v(-11.33, 0.92) * mm, "end": v(-11.44, 0.89) * mm});
            skLineSegment(sketch, "E920", {"start": v(-11.44, 0.89) * mm, "end": v(-11.56, 0.86) * mm});
            skLineSegment(sketch, "E921", {"start": v(-11.56, 0.86) * mm, "end": v(-11.67, 0.83) * mm});
            skLineSegment(sketch, "E922", {"start": v(-11.67, 0.83) * mm, "end": v(-11.79, 0.8) * mm});
            skLineSegment(sketch, "E923", {"start": v(-11.79, 0.8) * mm, "end": v(-11.9, 0.76) * mm});
            skLineSegment(sketch, "E924", {"start": v(-11.9, 0.76) * mm, "end": v(-12.02, 0.73) * mm});
            skLineSegment(sketch, "E925", {"start": v(-12.02, 0.73) * mm, "end": v(-12.13, 0.69) * mm});
            skLineSegment(sketch, "E926", {"start": v(-12.13, 0.69) * mm, "end": v(-12.25, 0.65) * mm});
            skLineSegment(sketch, "E927", {"start": v(-12.25, 0.65) * mm, "end": v(-12.36, 0.6) * mm});
            skLineSegment(sketch, "E928", {"start": v(-12.36, 0.6) * mm, "end": v(-12.47, 0.57) * mm});
            skLineSegment(sketch, "E929", {"start": v(-12.47, 0.57) * mm, "end": v(-12.59, 0.52) * mm});
            skLineSegment(sketch, "E930", {"start": v(-12.59, 0.52) * mm, "end": v(-12.7, 0.48) * mm});
            skLineSegment(sketch, "E931", {"start": v(-12.7, 0.48) * mm, "end": v(-12.82, 0.43) * mm});
            skLineSegment(sketch, "E932", {"start": v(-12.82, 0.43) * mm, "end": v(-12.93, 0.38) * mm});
            skLineSegment(sketch, "E933", {"start": v(-12.93, 0.38) * mm, "end": v(-13.04, 0.33) * mm});
            skLineSegment(sketch, "E934", {"start": v(-13.04, 0.33) * mm, "end": v(-13.06, 0.32) * mm});
            skLineSegment(sketch, "E935", {"start": v(-13.06, 0.32) * mm, "end": v(-13.06, -0.23) * mm});
            skLineSegment(sketch, "E936", {"start": v(-13.06, -0.23) * mm, "end": v(-13.03, -0.25) * mm});
            skLineSegment(sketch, "E937", {"start": v(-13.03, -0.25) * mm, "end": v(-12.91, -0.31) * mm});
            skLineSegment(sketch, "E938", {"start": v(-12.91, -0.31) * mm, "end": v(-12.8, -0.37) * mm});
            skLineSegment(sketch, "E939", {"start": v(-12.8, -0.37) * mm, "end": v(-12.68, -0.42) * mm});
            skLineSegment(sketch, "E940", {"start": v(-12.68, -0.42) * mm, "end": v(-12.57, -0.48) * mm});
            skLineSegment(sketch, "E941", {"start": v(-12.57, -0.48) * mm, "end": v(-12.46, -0.53) * mm});
            skLineSegment(sketch, "E942", {"start": v(-12.46, -0.53) * mm, "end": v(-12.34, -0.58) * mm});
            skLineSegment(sketch, "E943", {"start": v(-12.34, -0.58) * mm, "end": v(-12.23, -0.63) * mm});
            skLineSegment(sketch, "E944", {"start": v(-12.23, -0.63) * mm, "end": v(-12.12, -0.67) * mm});
            skLineSegment(sketch, "E945", {"start": v(-12.12, -0.67) * mm, "end": v(-12, -0.71) * mm});
            skLineSegment(sketch, "E946", {"start": v(-12, -0.71) * mm, "end": v(-11.89, -0.76) * mm});
            skLineSegment(sketch, "E947", {"start": v(-11.89, -0.76) * mm, "end": v(-11.77, -0.8) * mm});
            skLineSegment(sketch, "E948", {"start": v(-11.77, -0.8) * mm, "end": v(-11.66, -0.83) * mm});
            skLineSegment(sketch, "E949", {"start": v(-11.66, -0.83) * mm, "end": v(-11.55, -0.87) * mm});
            skLineSegment(sketch, "E950", {"start": v(-11.55, -0.87) * mm, "end": v(-11.43, -0.9) * mm});
            skLineSegment(sketch, "E951", {"start": v(-11.43, -0.9) * mm, "end": v(-11.32, -0.93) * mm});
            skLineSegment(sketch, "E952", {"start": v(-11.32, -0.93) * mm, "end": v(-11.2, -0.96) * mm});
            skLineSegment(sketch, "E953", {"start": v(-11.2, -0.96) * mm, "end": v(-11.09, -1) * mm});
            skLineSegment(sketch, "E954", {"start": v(-11.09, -1) * mm, "end": v(-10.98, -1.02) * mm});
            skLineSegment(sketch, "E955", {"start": v(-10.98, -1.02) * mm, "end": v(-10.86, -1.04) * mm});
            skLineSegment(sketch, "E956", {"start": v(-10.86, -1.04) * mm, "end": v(-10.75, -1.06) * mm});
            skLineSegment(sketch, "E957", {"start": v(-10.75, -1.06) * mm, "end": v(-10.63, -1.08) * mm});
            skLineSegment(sketch, "E958", {"start": v(-10.63, -1.08) * mm, "end": v(-10.52, -1.1) * mm});
            skLineSegment(sketch, "E959", {"start": v(-10.52, -1.1) * mm, "end": v(-10.4, -1.11) * mm});
            skLineSegment(sketch, "E960", {"start": v(-10.4, -1.11) * mm, "end": v(-10.29, -1.13) * mm});
            skLineSegment(sketch, "E961", {"start": v(-10.29, -1.13) * mm, "end": v(-10.17, -1.14) * mm});
            skLineSegment(sketch, "E962", {"start": v(-10.17, -1.14) * mm, "end": v(-10.06, -1.15) * mm});
            skLineSegment(sketch, "E963", {"start": v(-10.06, -1.15) * mm, "end": v(-9.94, -1.15) * mm});
            skLineSegment(sketch, "E964", {"start": v(-9.94, -1.15) * mm, "end": v(-9.83, -1.16) * mm});
            skLineSegment(sketch, "E965", {"start": v(-9.83, -1.16) * mm, "end": v(-9.71, -1.16) * mm});
            skLineSegment(sketch, "E966", {"start": v(-9.71, -1.16) * mm, "end": v(-9.6, -1.16) * mm});
            skLineSegment(sketch, "E967", {"start": v(-9.6, -1.16) * mm, "end": v(-9.48, -1.16) * mm});
            skLineSegment(sketch, "E968", {"start": v(-1.14, -16.04) * mm, "end": v(-1.23, -15.83) * mm});
            skLineSegment(sketch, "E969", {"start": v(-1.23, -15.83) * mm, "end": v(-1.32, -15.61) * mm});
            skLineSegment(sketch, "E970", {"start": v(-1.32, -15.61) * mm, "end": v(-1.4, -15.4) * mm});
            skLineSegment(sketch, "E971", {"start": v(-1.4, -15.4) * mm, "end": v(-1.48, -15.19) * mm});
            skLineSegment(sketch, "E972", {"start": v(-1.48, -15.19) * mm, "end": v(-1.56, -14.97) * mm});
            skLineSegment(sketch, "E973", {"start": v(-1.56, -14.97) * mm, "end": v(-1.63, -14.76) * mm});
            skLineSegment(sketch, "E974", {"start": v(-1.63, -14.76) * mm, "end": v(-1.7, -14.54) * mm});
            skLineSegment(sketch, "E975", {"start": v(-1.7, -14.54) * mm, "end": v(-1.77, -14.33) * mm});
            skLineSegment(sketch, "E976", {"start": v(-1.77, -14.33) * mm, "end": v(-1.84, -14.11) * mm});
            skLineSegment(sketch, "E977", {"start": v(-1.84, -14.11) * mm, "end": v(-1.9, -13.9) * mm});
            skLineSegment(sketch, "E978", {"start": v(-1.9, -13.9) * mm, "end": v(-1.96, -13.68) * mm});
            skLineSegment(sketch, "E979", {"start": v(-1.96, -13.68) * mm, "end": v(-2.01, -13.47) * mm});
            skLineSegment(sketch, "E980", {"start": v(-2.01, -13.47) * mm, "end": v(-2.07, -13.25) * mm});
            skLineSegment(sketch, "E981", {"start": v(-2.07, -13.25) * mm, "end": v(-2.12, -13.04) * mm});
            skLineSegment(sketch, "E982", {"start": v(-2.12, -13.04) * mm, "end": v(-2.17, -12.82) * mm});
            skLineSegment(sketch, "E983", {"start": v(-2.17, -12.82) * mm, "end": v(-2.21, -12.6) * mm});
            skLineSegment(sketch, "E984", {"start": v(-2.21, -12.6) * mm, "end": v(-2.25, -12.39) * mm});
            skLineSegment(sketch, "E985", {"start": v(-2.25, -12.39) * mm, "end": v(-2.3, -12.17) * mm});
            skLineSegment(sketch, "E986", {"start": v(-2.3, -12.17) * mm, "end": v(-2.33, -11.96) * mm});
            skLineSegment(sketch, "E987", {"start": v(-2.33, -11.96) * mm, "end": v(-2.36, -11.74) * mm});
            skLineSegment(sketch, "E988", {"start": v(-2.36, -11.74) * mm, "end": v(-2.39, -11.52) * mm});
            skLineSegment(sketch, "E989", {"start": v(-2.39, -11.52) * mm, "end": v(-2.41, -11.3) * mm});
            skLineSegment(sketch, "E990", {"start": v(-2.41, -11.3) * mm, "end": v(-2.44, -11.09) * mm});
            skLineSegment(sketch, "E991", {"start": v(-2.44, -11.09) * mm, "end": v(-2.46, -10.87) * mm});
            skLineSegment(sketch, "E992", {"start": v(-2.46, -10.87) * mm, "end": v(-2.47, -10.65) * mm});
            skLineSegment(sketch, "E993", {"start": v(-2.47, -10.65) * mm, "end": v(-2.49, -10.43) * mm});
            skLineSegment(sketch, "E994", {"start": v(-2.49, -10.43) * mm, "end": v(-2.5, -10.22) * mm});
            skLineSegment(sketch, "E995", {"start": v(-2.5, -10.22) * mm, "end": v(-2.5, -10) * mm});
            skLineSegment(sketch, "E996", {"start": v(-2.5, -10) * mm, "end": v(-2.51, -9.78) * mm});
            skLineSegment(sketch, "E997", {"start": v(-2.51, -9.78) * mm, "end": v(-2.51, -9.56) * mm});
            skLineSegment(sketch, "E998", {"start": v(-2.51, -9.56) * mm, "end": v(-2.51, -9.34) * mm});
            skLineSegment(sketch, "E999", {"start": v(-2.51, -9.34) * mm, "end": v(-2.5, -9.13) * mm});
            skLineSegment(sketch, "E1000", {"start": v(-2.5, -9.13) * mm, "end": v(-2.5, -8.91) * mm});
            skLineSegment(sketch, "E1001", {"start": v(-2.5, -8.91) * mm, "end": v(-2.49, -8.7) * mm});
            skLineSegment(sketch, "E1002", {"start": v(-2.49, -8.7) * mm, "end": v(-2.47, -8.48) * mm});
            skLineSegment(sketch, "E1003", {"start": v(-2.47, -8.48) * mm, "end": v(-2.46, -8.27) * mm});
            skLineSegment(sketch, "E1004", {"start": v(-2.46, -8.27) * mm, "end": v(-2.44, -8.05) * mm});
            skLineSegment(sketch, "E1005", {"start": v(-2.44, -8.05) * mm, "end": v(-2.42, -7.84) * mm});
            skLineSegment(sketch, "E1006", {"start": v(-2.42, -7.84) * mm, "end": v(-2.4, -7.62) * mm});
            skLineSegment(sketch, "E1007", {"start": v(-2.4, -7.62) * mm, "end": v(-2.36, -7.4) * mm});
            skLineSegment(sketch, "E1008", {"start": v(-2.36, -7.4) * mm, "end": v(-2.33, -7.2) * mm});
            skLineSegment(sketch, "E1009", {"start": v(-2.33, -7.2) * mm, "end": v(-2.3, -6.98) * mm});
            skLineSegment(sketch, "E1010", {"start": v(-2.3, -6.98) * mm, "end": v(-2.26, -6.77) * mm});
            skLineSegment(sketch, "E1011", {"start": v(-2.26, -6.77) * mm, "end": v(-2.22, -6.56) * mm});
            skLineSegment(sketch, "E1012", {"start": v(-2.22, -6.56) * mm, "end": v(-2.18, -6.34) * mm});
            skLineSegment(sketch, "E1013", {"start": v(-2.18, -6.34) * mm, "end": v(-2.13, -6.13) * mm});
            skLineSegment(sketch, "E1014", {"start": v(-2.13, -6.13) * mm, "end": v(-2.08, -5.92) * mm});
            skLineSegment(sketch, "E1015", {"start": v(-2.08, -5.92) * mm, "end": v(-2.03, -5.7) * mm});
            skLineSegment(sketch, "E1016", {"start": v(-2.03, -5.7) * mm, "end": v(-1.97, -5.5) * mm});
            skLineSegment(sketch, "E1017", {"start": v(-1.97, -5.5) * mm, "end": v(-1.92, -5.28) * mm});
            skLineSegment(sketch, "E1018", {"start": v(-1.92, -5.28) * mm, "end": v(-1.85, -5.07) * mm});
            skLineSegment(sketch, "E1019", {"start": v(-1.85, -5.07) * mm, "end": v(-1.8, -4.86) * mm});
            skLineSegment(sketch, "E1020", {"start": v(-1.8, -4.86) * mm, "end": v(-1.72, -4.64) * mm});
            skLineSegment(sketch, "E1021", {"start": v(-1.72, -4.64) * mm, "end": v(-1.66, -4.43) * mm});
            skLineSegment(sketch, "E1022", {"start": v(-1.66, -4.43) * mm, "end": v(-1.58, -4.22) * mm});
            skLineSegment(sketch, "E1023", {"start": v(-1.58, -4.22) * mm, "end": v(-1.5, -4.01) * mm});
            skLineSegment(sketch, "E1024", {"start": v(-1.5, -4.01) * mm, "end": v(-1.43, -3.8) * mm});
            skLineSegment(sketch, "E1025", {"start": v(-1.43, -3.8) * mm, "end": v(-1.35, -3.6) * mm});
            skLineSegment(sketch, "E1026", {"start": v(-1.35, -3.6) * mm, "end": v(-1.26, -3.38) * mm});
            skLineSegment(sketch, "E1027", {"start": v(-1.26, -3.38) * mm, "end": v(-1.18, -3.17) * mm});
            skLineSegment(sketch, "E1028", {"start": v(-1.18, -3.17) * mm, "end": v(-1.12, -3.02) * mm});
            skLineSegment(sketch, "E1029", {"start": v(-1.12, -3.02) * mm, "end": v(-1.19, -3) * mm});
            skLineSegment(sketch, "E1030", {"start": v(-1.19, -3) * mm, "end": v(-1.37, -2.92) * mm});
            skLineSegment(sketch, "E1031", {"start": v(-1.37, -2.92) * mm, "end": v(-1.55, -2.83) * mm});
            skLineSegment(sketch, "E1032", {"start": v(-1.55, -2.83) * mm, "end": v(-1.73, -2.72) * mm});
            skLineSegment(sketch, "E1033", {"start": v(-1.73, -2.72) * mm, "end": v(-1.9, -2.6) * mm});
            skLineSegment(sketch, "E1034", {"start": v(-1.9, -2.6) * mm, "end": v(-2.06, -2.48) * mm});
            skLineSegment(sketch, "E1035", {"start": v(-2.06, -2.48) * mm, "end": v(-2.2, -2.35) * mm});
            skLineSegment(sketch, "E1036", {"start": v(-2.2, -2.35) * mm, "end": v(-2.35, -2.2) * mm});
            skLineSegment(sketch, "E1037", {"start": v(-2.35, -2.2) * mm, "end": v(-2.48, -2.06) * mm});
            skLineSegment(sketch, "E1038", {"start": v(-2.48, -2.06) * mm, "end": v(-2.6, -1.9) * mm});
            skLineSegment(sketch, "E1039", {"start": v(-2.6, -1.9) * mm, "end": v(-2.72, -1.73) * mm});
            skLineSegment(sketch, "E1040", {"start": v(-2.72, -1.73) * mm, "end": v(-2.83, -1.55) * mm});
            skLineSegment(sketch, "E1041", {"start": v(-2.83, -1.55) * mm, "end": v(-2.92, -1.37) * mm});
            skLineSegment(sketch, "E1042", {"start": v(-2.92, -1.37) * mm, "end": v(-3, -1.19) * mm});
            skLineSegment(sketch, "E1043", {"start": v(-3, -1.19) * mm, "end": v(-3.06, -1.02) * mm});
            skLineSegment(sketch, "E1044", {"start": v(-3.06, -1.02) * mm, "end": v(-3.17, -1.07) * mm});
            skLineSegment(sketch, "E1045", {"start": v(-3.17, -1.07) * mm, "end": v(-3.38, -1.17) * mm});
            skLineSegment(sketch, "E1046", {"start": v(-3.38, -1.17) * mm, "end": v(-3.6, -1.27) * mm});
            skLineSegment(sketch, "E1047", {"start": v(-3.6, -1.27) * mm, "end": v(-3.8, -1.36) * mm});
            skLineSegment(sketch, "E1048", {"start": v(-3.8, -1.36) * mm, "end": v(-4.01, -1.45) * mm});
            skLineSegment(sketch, "E1049", {"start": v(-4.01, -1.45) * mm, "end": v(-4.22, -1.54) * mm});
            skLineSegment(sketch, "E1050", {"start": v(-4.22, -1.54) * mm, "end": v(-4.43, -1.63) * mm});
            skLineSegment(sketch, "E1051", {"start": v(-4.43, -1.63) * mm, "end": v(-4.64, -1.7) * mm});
            skLineSegment(sketch, "E1052", {"start": v(-4.64, -1.7) * mm, "end": v(-4.86, -1.78) * mm});
            skLineSegment(sketch, "E1053", {"start": v(-4.86, -1.78) * mm, "end": v(-5.07, -1.86) * mm});
            skLineSegment(sketch, "E1054", {"start": v(-5.07, -1.86) * mm, "end": v(-5.28, -1.93) * mm});
            skLineSegment(sketch, "E1055", {"start": v(-5.28, -1.93) * mm, "end": v(-5.5, -2) * mm});
            skLineSegment(sketch, "E1056", {"start": v(-5.5, -2) * mm, "end": v(-5.7, -2.06) * mm});
            skLineSegment(sketch, "E1057", {"start": v(-5.7, -2.06) * mm, "end": v(-5.92, -2.12) * mm});
            skLineSegment(sketch, "E1058", {"start": v(-5.92, -2.12) * mm, "end": v(-6.13, -2.18) * mm});
            skLineSegment(sketch, "E1059", {"start": v(-6.13, -2.18) * mm, "end": v(-6.34, -2.23) * mm});
            skLineSegment(sketch, "E1060", {"start": v(-6.34, -2.23) * mm, "end": v(-6.56, -2.28) * mm});
            skLineSegment(sketch, "E1061", {"start": v(-6.56, -2.28) * mm, "end": v(-6.77, -2.33) * mm});
            skLineSegment(sketch, "E1062", {"start": v(-6.77, -2.33) * mm, "end": v(-6.98, -2.37) * mm});
            skLineSegment(sketch, "E1063", {"start": v(-6.98, -2.37) * mm, "end": v(-7.2, -2.41) * mm});
            skLineSegment(sketch, "E1064", {"start": v(-7.2, -2.41) * mm, "end": v(-7.4, -2.45) * mm});
            skLineSegment(sketch, "E1065", {"start": v(-7.4, -2.45) * mm, "end": v(-7.62, -2.48) * mm});
            skLineSegment(sketch, "E1066", {"start": v(-7.62, -2.48) * mm, "end": v(-7.84, -2.51) * mm});
            skLineSegment(sketch, "E1067", {"start": v(-7.84, -2.51) * mm, "end": v(-8.05, -2.54) * mm});
            skLineSegment(sketch, "E1068", {"start": v(-8.05, -2.54) * mm, "end": v(-8.27, -2.56) * mm});
            skLineSegment(sketch, "E1069", {"start": v(-8.27, -2.56) * mm, "end": v(-8.48, -2.58) * mm});
            skLineSegment(sketch, "E1070", {"start": v(-8.48, -2.58) * mm, "end": v(-8.7, -2.6) * mm});
            skLineSegment(sketch, "E1071", {"start": v(-8.7, -2.6) * mm, "end": v(-8.91, -2.6) * mm});
            skLineSegment(sketch, "E1072", {"start": v(-8.91, -2.6) * mm, "end": v(-9.13, -2.62) * mm});
            skLineSegment(sketch, "E1073", {"start": v(-9.13, -2.62) * mm, "end": v(-9.34, -2.62) * mm});
            skLineSegment(sketch, "E1074", {"start": v(-9.34, -2.62) * mm, "end": v(-9.56, -2.62) * mm});
            skLineSegment(sketch, "E1075", {"start": v(-9.56, -2.62) * mm, "end": v(-9.78, -2.62) * mm});
            skLineSegment(sketch, "E1076", {"start": v(-9.78, -2.62) * mm, "end": v(-10, -2.62) * mm});
            skLineSegment(sketch, "E1077", {"start": v(-10, -2.62) * mm, "end": v(-10.22, -2.6) * mm});
            skLineSegment(sketch, "E1078", {"start": v(-10.22, -2.6) * mm, "end": v(-10.43, -2.6) * mm});
            skLineSegment(sketch, "E1079", {"start": v(-10.43, -2.6) * mm, "end": v(-10.65, -2.58) * mm});
            skLineSegment(sketch, "E1080", {"start": v(-10.65, -2.58) * mm, "end": v(-10.87, -2.56) * mm});
            skLineSegment(sketch, "E1081", {"start": v(-10.87, -2.56) * mm, "end": v(-11.09, -2.54) * mm});
            skLineSegment(sketch, "E1082", {"start": v(-11.09, -2.54) * mm, "end": v(-11.3, -2.5) * mm});
            skLineSegment(sketch, "E1083", {"start": v(-11.3, -2.5) * mm, "end": v(-11.52, -2.48) * mm});
            skLineSegment(sketch, "E1084", {"start": v(-11.52, -2.48) * mm, "end": v(-11.74, -2.44) * mm});
            skLineSegment(sketch, "E1085", {"start": v(-11.74, -2.44) * mm, "end": v(-11.96, -2.4) * mm});
            skLineSegment(sketch, "E1086", {"start": v(-11.96, -2.4) * mm, "end": v(-12.17, -2.37) * mm});
            skLineSegment(sketch, "E1087", {"start": v(-12.17, -2.37) * mm, "end": v(-12.39, -2.32) * mm});
            skLineSegment(sketch, "E1088", {"start": v(-12.39, -2.32) * mm, "end": v(-12.6, -2.27) * mm});
            skLineSegment(sketch, "E1089", {"start": v(-12.6, -2.27) * mm, "end": v(-12.82, -2.22) * mm});
            skLineSegment(sketch, "E1090", {"start": v(-12.82, -2.22) * mm, "end": v(-13.04, -2.17) * mm});
            skLineSegment(sketch, "E1091", {"start": v(-13.04, -2.17) * mm, "end": v(-13.25, -2.1) * mm});
            skLineSegment(sketch, "E1092", {"start": v(-13.25, -2.1) * mm, "end": v(-13.47, -2.04) * mm});
            skLineSegment(sketch, "E1093", {"start": v(-13.47, -2.04) * mm, "end": v(-13.68, -1.98) * mm});
            skLineSegment(sketch, "E1094", {"start": v(-13.68, -1.98) * mm, "end": v(-13.9, -1.9) * mm});
            skLineSegment(sketch, "E1095", {"start": v(-13.9, -1.9) * mm, "end": v(-14.11, -1.84) * mm});
            skLineSegment(sketch, "E1096", {"start": v(-14.11, -1.84) * mm, "end": v(-14.33, -1.76) * mm});
            skLineSegment(sketch, "E1097", {"start": v(-14.33, -1.76) * mm, "end": v(-14.54, -1.68) * mm});
            skLineSegment(sketch, "E1098", {"start": v(-14.54, -1.68) * mm, "end": v(-14.76, -1.6) * mm});
            skLineSegment(sketch, "E1099", {"start": v(-14.76, -1.6) * mm, "end": v(-14.97, -1.51) * mm});
            skLineSegment(sketch, "E1100", {"start": v(-14.97, -1.51) * mm, "end": v(-15.19, -1.42) * mm});
            skLineSegment(sketch, "E1101", {"start": v(-15.19, -1.42) * mm, "end": v(-15.4, -1.33) * mm});
            skLineSegment(sketch, "E1102", {"start": v(-15.4, -1.33) * mm, "end": v(-15.61, -1.23) * mm});
            skLineSegment(sketch, "E1103", {"start": v(-15.61, -1.23) * mm, "end": v(-15.83, -1.13) * mm});
            skLineSegment(sketch, "E1104", {"start": v(-15.83, -1.13) * mm, "end": v(-16.04, -1.03) * mm});
            skLineSegment(sketch, "E1105", {"start": v(-16.04, -1.03) * mm, "end": v(-16.17, -0.96) * mm});
            skLineSegment(sketch, "E1106", {"start": v(-16.17, -0.96) * mm, "end": v(-16.17, -1.02) * mm});
            skLineSegment(sketch, "E1107", {"start": v(-16.17, -1.02) * mm, "end": v(-16.07, -2.03) * mm});
            skLineSegment(sketch, "E1108", {"start": v(-16.07, -2.03) * mm, "end": v(-15.91, -3.04) * mm});
            skLineSegment(sketch, "E1109", {"start": v(-15.91, -3.04) * mm, "end": v(-15.69, -4.03) * mm});
            skLineSegment(sketch, "E1110", {"start": v(-15.69, -4.03) * mm, "end": v(-15.4, -5) * mm});
            skLineSegment(sketch, "E1111", {"start": v(-15.4, -5) * mm, "end": v(-15.06, -5.96) * mm});
            skLineSegment(sketch, "E1112", {"start": v(-15.06, -5.96) * mm, "end": v(-14.66, -6.9) * mm});
            skLineSegment(sketch, "E1113", {"start": v(-14.66, -6.9) * mm, "end": v(-14.2, -7.8) * mm});
            skLineSegment(sketch, "E1114", {"start": v(-14.2, -7.8) * mm, "end": v(-13.68, -8.68) * mm});
            skLineSegment(sketch, "E1115", {"start": v(-13.68, -8.68) * mm, "end": v(-13.1, -9.52) * mm});
            skLineSegment(sketch, "E1116", {"start": v(-13.1, -9.52) * mm, "end": v(-12.48, -10.32) * mm});
            skLineSegment(sketch, "E1117", {"start": v(-12.48, -10.32) * mm, "end": v(-11.8, -11.09) * mm});
            skLineSegment(sketch, "E1118", {"start": v(-11.8, -11.09) * mm, "end": v(-11.09, -11.8) * mm});
            skLineSegment(sketch, "E1119", {"start": v(-11.09, -11.8) * mm, "end": v(-10.32, -12.48) * mm});
            skLineSegment(sketch, "E1120", {"start": v(-10.32, -12.48) * mm, "end": v(-9.52, -13.1) * mm});
            skLineSegment(sketch, "E1121", {"start": v(-9.52, -13.1) * mm, "end": v(-8.68, -13.68) * mm});
            skLineSegment(sketch, "E1122", {"start": v(-8.68, -13.68) * mm, "end": v(-7.8, -14.2) * mm});
            skLineSegment(sketch, "E1123", {"start": v(-7.8, -14.2) * mm, "end": v(-6.9, -14.66) * mm});
            skLineSegment(sketch, "E1124", {"start": v(-6.9, -14.66) * mm, "end": v(-5.96, -15.06) * mm});
            skLineSegment(sketch, "E1125", {"start": v(-5.96, -15.06) * mm, "end": v(-5, -15.4) * mm});
            skLineSegment(sketch, "E1126", {"start": v(-5, -15.4) * mm, "end": v(-4.03, -15.69) * mm});
            skLineSegment(sketch, "E1127", {"start": v(-4.03, -15.69) * mm, "end": v(-3.04, -15.91) * mm});
            skLineSegment(sketch, "E1128", {"start": v(-3.04, -15.91) * mm, "end": v(-2.03, -16.07) * mm});
            skLineSegment(sketch, "E1129", {"start": v(-2.03, -16.07) * mm, "end": v(-1.09, -16.16) * mm});
            skLineSegment(sketch, "E1130", {"start": v(-1.09, -16.16) * mm, "end": v(-1.14, -16.04) * mm});
            skLineSegment(sketch, "E1131", {"start": v(1.02, -16.17) * mm, "end": v(2.03, -16.07) * mm});
            skLineSegment(sketch, "E1132", {"start": v(2.03, -16.07) * mm, "end": v(3.04, -15.91) * mm});
            skLineSegment(sketch, "E1133", {"start": v(3.04, -15.91) * mm, "end": v(4.03, -15.69) * mm});
            skLineSegment(sketch, "E1134", {"start": v(4.03, -15.69) * mm, "end": v(5, -15.4) * mm});
            skLineSegment(sketch, "E1135", {"start": v(5, -15.4) * mm, "end": v(5.96, -15.06) * mm});
            skLineSegment(sketch, "E1136", {"start": v(5.96, -15.06) * mm, "end": v(6.9, -14.66) * mm});
            skLineSegment(sketch, "E1137", {"start": v(6.9, -14.66) * mm, "end": v(7.8, -14.2) * mm});
            skLineSegment(sketch, "E1138", {"start": v(7.8, -14.2) * mm, "end": v(8.68, -13.68) * mm});
            skLineSegment(sketch, "E1139", {"start": v(8.68, -13.68) * mm, "end": v(9.52, -13.1) * mm});
            skLineSegment(sketch, "E1140", {"start": v(9.52, -13.1) * mm, "end": v(10.32, -12.48) * mm});
            skLineSegment(sketch, "E1141", {"start": v(10.32, -12.48) * mm, "end": v(11.09, -11.8) * mm});
            skLineSegment(sketch, "E1142", {"start": v(11.09, -11.8) * mm, "end": v(11.8, -11.09) * mm});
            skLineSegment(sketch, "E1143", {"start": v(11.8, -11.09) * mm, "end": v(12.48, -10.32) * mm});
            skLineSegment(sketch, "E1144", {"start": v(12.48, -10.32) * mm, "end": v(13.1, -9.52) * mm});
            skLineSegment(sketch, "E1145", {"start": v(13.1, -9.52) * mm, "end": v(13.68, -8.68) * mm});
            skLineSegment(sketch, "E1146", {"start": v(13.68, -8.68) * mm, "end": v(14.2, -7.8) * mm});
            skLineSegment(sketch, "E1147", {"start": v(14.2, -7.8) * mm, "end": v(14.66, -6.9) * mm});
            skLineSegment(sketch, "E1148", {"start": v(14.66, -6.9) * mm, "end": v(15.06, -5.96) * mm});
            skLineSegment(sketch, "E1149", {"start": v(15.06, -5.96) * mm, "end": v(15.4, -5) * mm});
            skLineSegment(sketch, "E1150", {"start": v(15.4, -5) * mm, "end": v(15.69, -4.03) * mm});
            skLineSegment(sketch, "E1151", {"start": v(15.69, -4.03) * mm, "end": v(15.91, -3.04) * mm});
            skLineSegment(sketch, "E1152", {"start": v(15.91, -3.04) * mm, "end": v(16.07, -2.03) * mm});
            skLineSegment(sketch, "E1153", {"start": v(16.07, -2.03) * mm, "end": v(16.16, -1.09) * mm});
            skLineSegment(sketch, "E1154", {"start": v(16.16, -1.09) * mm, "end": v(16.04, -1.14) * mm});
            skLineSegment(sketch, "E1155", {"start": v(16.04, -1.14) * mm, "end": v(15.83, -1.23) * mm});
            skLineSegment(sketch, "E1156", {"start": v(15.83, -1.23) * mm, "end": v(15.61, -1.32) * mm});
            skLineSegment(sketch, "E1157", {"start": v(15.61, -1.32) * mm, "end": v(15.4, -1.4) * mm});
            skLineSegment(sketch, "E1158", {"start": v(15.4, -1.4) * mm, "end": v(15.19, -1.48) * mm});
            skLineSegment(sketch, "E1159", {"start": v(15.19, -1.48) * mm, "end": v(14.97, -1.56) * mm});
            skLineSegment(sketch, "E1160", {"start": v(14.97, -1.56) * mm, "end": v(14.76, -1.63) * mm});
            skLineSegment(sketch, "E1161", {"start": v(14.76, -1.63) * mm, "end": v(14.54, -1.7) * mm});
            skLineSegment(sketch, "E1162", {"start": v(14.54, -1.7) * mm, "end": v(14.33, -1.77) * mm});
            skLineSegment(sketch, "E1163", {"start": v(14.33, -1.77) * mm, "end": v(14.11, -1.84) * mm});
            skLineSegment(sketch, "E1164", {"start": v(14.11, -1.84) * mm, "end": v(13.9, -1.9) * mm});
            skLineSegment(sketch, "E1165", {"start": v(13.9, -1.9) * mm, "end": v(13.68, -1.96) * mm});
            skLineSegment(sketch, "E1166", {"start": v(13.68, -1.96) * mm, "end": v(13.47, -2.01) * mm});
            skLineSegment(sketch, "E1167", {"start": v(13.47, -2.01) * mm, "end": v(13.25, -2.07) * mm});
            skLineSegment(sketch, "E1168", {"start": v(13.25, -2.07) * mm, "end": v(13.04, -2.12) * mm});
            skLineSegment(sketch, "E1169", {"start": v(13.04, -2.12) * mm, "end": v(12.82, -2.17) * mm});
            skLineSegment(sketch, "E1170", {"start": v(12.82, -2.17) * mm, "end": v(12.6, -2.21) * mm});
            skLineSegment(sketch, "E1171", {"start": v(12.6, -2.21) * mm, "end": v(12.39, -2.25) * mm});
            skLineSegment(sketch, "E1172", {"start": v(12.39, -2.25) * mm, "end": v(12.17, -2.3) * mm});
            skLineSegment(sketch, "E1173", {"start": v(12.17, -2.3) * mm, "end": v(11.96, -2.33) * mm});
            skLineSegment(sketch, "E1174", {"start": v(11.96, -2.33) * mm, "end": v(11.74, -2.36) * mm});
            skLineSegment(sketch, "E1175", {"start": v(11.74, -2.36) * mm, "end": v(11.52, -2.39) * mm});
            skLineSegment(sketch, "E1176", {"start": v(11.52, -2.39) * mm, "end": v(11.3, -2.41) * mm});
            skLineSegment(sketch, "E1177", {"start": v(11.3, -2.41) * mm, "end": v(11.09, -2.44) * mm});
            skLineSegment(sketch, "E1178", {"start": v(11.09, -2.44) * mm, "end": v(10.87, -2.46) * mm});
            skLineSegment(sketch, "E1179", {"start": v(10.87, -2.46) * mm, "end": v(10.65, -2.47) * mm});
            skLineSegment(sketch, "E1180", {"start": v(10.65, -2.47) * mm, "end": v(10.43, -2.49) * mm});
            skLineSegment(sketch, "E1181", {"start": v(10.43, -2.49) * mm, "end": v(10.22, -2.5) * mm});
            skLineSegment(sketch, "E1182", {"start": v(10.22, -2.5) * mm, "end": v(10, -2.5) * mm});
            skLineSegment(sketch, "E1183", {"start": v(10, -2.5) * mm, "end": v(9.78, -2.51) * mm});
            skLineSegment(sketch, "E1184", {"start": v(9.78, -2.51) * mm, "end": v(9.56, -2.51) * mm});
            skLineSegment(sketch, "E1185", {"start": v(9.56, -2.51) * mm, "end": v(9.34, -2.51) * mm});
            skLineSegment(sketch, "E1186", {"start": v(9.34, -2.51) * mm, "end": v(9.13, -2.5) * mm});
            skLineSegment(sketch, "E1187", {"start": v(9.13, -2.5) * mm, "end": v(8.91, -2.5) * mm});
            skLineSegment(sketch, "E1188", {"start": v(8.91, -2.5) * mm, "end": v(8.7, -2.49) * mm});
            skLineSegment(sketch, "E1189", {"start": v(8.7, -2.49) * mm, "end": v(8.48, -2.47) * mm});
            skLineSegment(sketch, "E1190", {"start": v(8.48, -2.47) * mm, "end": v(8.27, -2.46) * mm});
            skLineSegment(sketch, "E1191", {"start": v(8.27, -2.46) * mm, "end": v(8.05, -2.44) * mm});
            skLineSegment(sketch, "E1192", {"start": v(8.05, -2.44) * mm, "end": v(7.84, -2.42) * mm});
            skLineSegment(sketch, "E1193", {"start": v(7.84, -2.42) * mm, "end": v(7.62, -2.4) * mm});
            skLineSegment(sketch, "E1194", {"start": v(7.62, -2.4) * mm, "end": v(7.4, -2.36) * mm});
            skLineSegment(sketch, "E1195", {"start": v(7.4, -2.36) * mm, "end": v(7.2, -2.33) * mm});
            skLineSegment(sketch, "E1196", {"start": v(7.2, -2.33) * mm, "end": v(6.98, -2.3) * mm});
            skLineSegment(sketch, "E1197", {"start": v(6.98, -2.3) * mm, "end": v(6.77, -2.26) * mm});
            skLineSegment(sketch, "E1198", {"start": v(6.77, -2.26) * mm, "end": v(6.56, -2.22) * mm});
            skLineSegment(sketch, "E1199", {"start": v(6.56, -2.22) * mm, "end": v(6.34, -2.18) * mm});
            skLineSegment(sketch, "E1200", {"start": v(6.34, -2.18) * mm, "end": v(6.13, -2.13) * mm});
            skLineSegment(sketch, "E1201", {"start": v(6.13, -2.13) * mm, "end": v(5.92, -2.08) * mm});
            skLineSegment(sketch, "E1202", {"start": v(5.92, -2.08) * mm, "end": v(5.7, -2.03) * mm});
            skLineSegment(sketch, "E1203", {"start": v(5.7, -2.03) * mm, "end": v(5.5, -1.97) * mm});
            skLineSegment(sketch, "E1204", {"start": v(5.5, -1.97) * mm, "end": v(5.28, -1.92) * mm});
            skLineSegment(sketch, "E1205", {"start": v(5.28, -1.92) * mm, "end": v(5.07, -1.85) * mm});
            skLineSegment(sketch, "E1206", {"start": v(5.07, -1.85) * mm, "end": v(4.86, -1.8) * mm});
            skLineSegment(sketch, "E1207", {"start": v(4.86, -1.8) * mm, "end": v(4.64, -1.72) * mm});
            skLineSegment(sketch, "E1208", {"start": v(4.64, -1.72) * mm, "end": v(4.43, -1.66) * mm});
            skLineSegment(sketch, "E1209", {"start": v(4.43, -1.66) * mm, "end": v(4.22, -1.58) * mm});
            skLineSegment(sketch, "E1210", {"start": v(4.22, -1.58) * mm, "end": v(4.01, -1.5) * mm});
            skLineSegment(sketch, "E1211", {"start": v(4.01, -1.5) * mm, "end": v(3.8, -1.43) * mm});
            skLineSegment(sketch, "E1212", {"start": v(3.8, -1.43) * mm, "end": v(3.6, -1.35) * mm});
            skLineSegment(sketch, "E1213", {"start": v(3.6, -1.35) * mm, "end": v(3.38, -1.26) * mm});
            skLineSegment(sketch, "E1214", {"start": v(3.38, -1.26) * mm, "end": v(3.17, -1.18) * mm});
            skLineSegment(sketch, "E1215", {"start": v(3.17, -1.18) * mm, "end": v(3.02, -1.12) * mm});
            skLineSegment(sketch, "E1216", {"start": v(3.02, -1.12) * mm, "end": v(3, -1.19) * mm});
            skLineSegment(sketch, "E1217", {"start": v(3, -1.19) * mm, "end": v(2.92, -1.37) * mm});
            skLineSegment(sketch, "E1218", {"start": v(2.92, -1.37) * mm, "end": v(2.83, -1.55) * mm});
            skLineSegment(sketch, "E1219", {"start": v(2.83, -1.55) * mm, "end": v(2.72, -1.73) * mm});
            skLineSegment(sketch, "E1220", {"start": v(2.72, -1.73) * mm, "end": v(2.6, -1.9) * mm});
            skLineSegment(sketch, "E1221", {"start": v(2.6, -1.9) * mm, "end": v(2.48, -2.06) * mm});
            skLineSegment(sketch, "E1222", {"start": v(2.48, -2.06) * mm, "end": v(2.35, -2.2) * mm});
            skLineSegment(sketch, "E1223", {"start": v(2.35, -2.2) * mm, "end": v(2.2, -2.35) * mm});
            skLineSegment(sketch, "E1224", {"start": v(2.2, -2.35) * mm, "end": v(2.06, -2.48) * mm});
            skLineSegment(sketch, "E1225", {"start": v(2.06, -2.48) * mm, "end": v(1.9, -2.6) * mm});
            skLineSegment(sketch, "E1226", {"start": v(1.9, -2.6) * mm, "end": v(1.73, -2.72) * mm});
            skLineSegment(sketch, "E1227", {"start": v(1.73, -2.72) * mm, "end": v(1.55, -2.83) * mm});
            skLineSegment(sketch, "E1228", {"start": v(1.55, -2.83) * mm, "end": v(1.37, -2.92) * mm});
            skLineSegment(sketch, "E1229", {"start": v(1.37, -2.92) * mm, "end": v(1.19, -3) * mm});
            skLineSegment(sketch, "E1230", {"start": v(1.19, -3) * mm, "end": v(1.02, -3.06) * mm});
            skLineSegment(sketch, "E1231", {"start": v(1.02, -3.06) * mm, "end": v(1.07, -3.17) * mm});
            skLineSegment(sketch, "E1232", {"start": v(1.07, -3.17) * mm, "end": v(1.17, -3.38) * mm});
            skLineSegment(sketch, "E1233", {"start": v(1.17, -3.38) * mm, "end": v(1.27, -3.6) * mm});
            skLineSegment(sketch, "E1234", {"start": v(1.27, -3.6) * mm, "end": v(1.36, -3.8) * mm});
            skLineSegment(sketch, "E1235", {"start": v(1.36, -3.8) * mm, "end": v(1.45, -4.01) * mm});
            skLineSegment(sketch, "E1236", {"start": v(1.45, -4.01) * mm, "end": v(1.54, -4.22) * mm});
            skLineSegment(sketch, "E1237", {"start": v(1.54, -4.22) * mm, "end": v(1.63, -4.43) * mm});
            skLineSegment(sketch, "E1238", {"start": v(1.63, -4.43) * mm, "end": v(1.7, -4.64) * mm});
            skLineSegment(sketch, "E1239", {"start": v(1.7, -4.64) * mm, "end": v(1.78, -4.86) * mm});
            skLineSegment(sketch, "E1240", {"start": v(1.78, -4.86) * mm, "end": v(1.86, -5.07) * mm});
            skLineSegment(sketch, "E1241", {"start": v(1.86, -5.07) * mm, "end": v(1.93, -5.28) * mm});
            skLineSegment(sketch, "E1242", {"start": v(1.93, -5.28) * mm, "end": v(2, -5.5) * mm});
            skLineSegment(sketch, "E1243", {"start": v(2, -5.5) * mm, "end": v(2.06, -5.7) * mm});
            skLineSegment(sketch, "E1244", {"start": v(2.06, -5.7) * mm, "end": v(2.12, -5.92) * mm});
            skLineSegment(sketch, "E1245", {"start": v(2.12, -5.92) * mm, "end": v(2.18, -6.13) * mm});
            skLineSegment(sketch, "E1246", {"start": v(2.18, -6.13) * mm, "end": v(2.23, -6.34) * mm});
            skLineSegment(sketch, "E1247", {"start": v(2.23, -6.34) * mm, "end": v(2.28, -6.56) * mm});
            skLineSegment(sketch, "E1248", {"start": v(2.28, -6.56) * mm, "end": v(2.33, -6.77) * mm});
            skLineSegment(sketch, "E1249", {"start": v(2.33, -6.77) * mm, "end": v(2.37, -6.98) * mm});
            skLineSegment(sketch, "E1250", {"start": v(2.37, -6.98) * mm, "end": v(2.41, -7.2) * mm});
            skLineSegment(sketch, "E1251", {"start": v(2.41, -7.2) * mm, "end": v(2.45, -7.4) * mm});
            skLineSegment(sketch, "E1252", {"start": v(2.45, -7.4) * mm, "end": v(2.48, -7.62) * mm});
            skLineSegment(sketch, "E1253", {"start": v(2.48, -7.62) * mm, "end": v(2.51, -7.84) * mm});
            skLineSegment(sketch, "E1254", {"start": v(2.51, -7.84) * mm, "end": v(2.54, -8.05) * mm});
            skLineSegment(sketch, "E1255", {"start": v(2.54, -8.05) * mm, "end": v(2.56, -8.27) * mm});
            skLineSegment(sketch, "E1256", {"start": v(2.56, -8.27) * mm, "end": v(2.58, -8.48) * mm});
            skLineSegment(sketch, "E1257", {"start": v(2.58, -8.48) * mm, "end": v(2.6, -8.7) * mm});
            skLineSegment(sketch, "E1258", {"start": v(2.6, -8.7) * mm, "end": v(2.6, -8.91) * mm});
            skLineSegment(sketch, "E1259", {"start": v(2.6, -8.91) * mm, "end": v(2.62, -9.13) * mm});
            skLineSegment(sketch, "E1260", {"start": v(2.62, -9.13) * mm, "end": v(2.62, -9.34) * mm});
            skLineSegment(sketch, "E1261", {"start": v(2.62, -9.34) * mm, "end": v(2.62, -9.56) * mm});
            skLineSegment(sketch, "E1262", {"start": v(2.62, -9.56) * mm, "end": v(2.62, -9.78) * mm});
            skLineSegment(sketch, "E1263", {"start": v(2.62, -9.78) * mm, "end": v(2.62, -10) * mm});
            skLineSegment(sketch, "E1264", {"start": v(2.62, -10) * mm, "end": v(2.6, -10.22) * mm});
            skLineSegment(sketch, "E1265", {"start": v(2.6, -10.22) * mm, "end": v(2.6, -10.43) * mm});
            skLineSegment(sketch, "E1266", {"start": v(2.6, -10.43) * mm, "end": v(2.58, -10.65) * mm});
            skLineSegment(sketch, "E1267", {"start": v(2.58, -10.65) * mm, "end": v(2.56, -10.87) * mm});
            skLineSegment(sketch, "E1268", {"start": v(2.56, -10.87) * mm, "end": v(2.54, -11.09) * mm});
            skLineSegment(sketch, "E1269", {"start": v(2.54, -11.09) * mm, "end": v(2.5, -11.3) * mm});
            skLineSegment(sketch, "E1270", {"start": v(2.5, -11.3) * mm, "end": v(2.48, -11.52) * mm});
            skLineSegment(sketch, "E1271", {"start": v(2.48, -11.52) * mm, "end": v(2.44, -11.74) * mm});
            skLineSegment(sketch, "E1272", {"start": v(2.44, -11.74) * mm, "end": v(2.4, -11.96) * mm});
            skLineSegment(sketch, "E1273", {"start": v(2.4, -11.96) * mm, "end": v(2.37, -12.17) * mm});
            skLineSegment(sketch, "E1274", {"start": v(2.37, -12.17) * mm, "end": v(2.32, -12.39) * mm});
            skLineSegment(sketch, "E1275", {"start": v(2.32, -12.39) * mm, "end": v(2.27, -12.6) * mm});
            skLineSegment(sketch, "E1276", {"start": v(2.27, -12.6) * mm, "end": v(2.22, -12.82) * mm});
            skLineSegment(sketch, "E1277", {"start": v(2.22, -12.82) * mm, "end": v(2.17, -13.04) * mm});
            skLineSegment(sketch, "E1278", {"start": v(2.17, -13.04) * mm, "end": v(2.1, -13.25) * mm});
            skLineSegment(sketch, "E1279", {"start": v(2.1, -13.25) * mm, "end": v(2.04, -13.47) * mm});
            skLineSegment(sketch, "E1280", {"start": v(2.04, -13.47) * mm, "end": v(1.98, -13.68) * mm});
            skLineSegment(sketch, "E1281", {"start": v(1.98, -13.68) * mm, "end": v(1.9, -13.9) * mm});
            skLineSegment(sketch, "E1282", {"start": v(1.9, -13.9) * mm, "end": v(1.84, -14.11) * mm});
            skLineSegment(sketch, "E1283", {"start": v(1.84, -14.11) * mm, "end": v(1.76, -14.33) * mm});
            skLineSegment(sketch, "E1284", {"start": v(1.76, -14.33) * mm, "end": v(1.68, -14.54) * mm});
            skLineSegment(sketch, "E1285", {"start": v(1.68, -14.54) * mm, "end": v(1.6, -14.76) * mm});
            skLineSegment(sketch, "E1286", {"start": v(1.6, -14.76) * mm, "end": v(1.51, -14.97) * mm});
            skLineSegment(sketch, "E1287", {"start": v(1.51, -14.97) * mm, "end": v(1.42, -15.19) * mm});
            skLineSegment(sketch, "E1288", {"start": v(1.42, -15.19) * mm, "end": v(1.33, -15.4) * mm});
            skLineSegment(sketch, "E1289", {"start": v(1.33, -15.4) * mm, "end": v(1.23, -15.61) * mm});
            skLineSegment(sketch, "E1290", {"start": v(1.23, -15.61) * mm, "end": v(1.13, -15.83) * mm});
            skLineSegment(sketch, "E1291", {"start": v(1.13, -15.83) * mm, "end": v(1.03, -16.04) * mm});
            skLineSegment(sketch, "E1292", {"start": v(1.03, -16.04) * mm, "end": v(0.96, -16.17) * mm});
            skLineSegment(sketch, "E1293", {"start": v(0.96, -16.17) * mm, "end": v(1.02, -16.17) * mm});
            skLineSegment(sketch, "E1294", {"start": v(0.25, -13.03) * mm, "end": v(0.31, -12.91) * mm});
            skLineSegment(sketch, "E1295", {"start": v(0.31, -12.91) * mm, "end": v(0.37, -12.8) * mm});
            skLineSegment(sketch, "E1296", {"start": v(0.37, -12.8) * mm, "end": v(0.42, -12.68) * mm});
            skLineSegment(sketch, "E1297", {"start": v(0.42, -12.68) * mm, "end": v(0.48, -12.57) * mm});
            skLineSegment(sketch, "E1298", {"start": v(0.48, -12.57) * mm, "end": v(0.53, -12.46) * mm});
            skLineSegment(sketch, "E1299", {"start": v(0.53, -12.46) * mm, "end": v(0.58, -12.34) * mm});
            skLineSegment(sketch, "E1300", {"start": v(0.58, -12.34) * mm, "end": v(0.63, -12.23) * mm});
            skLineSegment(sketch, "E1301", {"start": v(0.63, -12.23) * mm, "end": v(0.67, -12.12) * mm});
            skLineSegment(sketch, "E1302", {"start": v(0.67, -12.12) * mm, "end": v(0.71, -12) * mm});
            skLineSegment(sketch, "E1303", {"start": v(0.71, -12) * mm, "end": v(0.76, -11.89) * mm});
            skLineSegment(sketch, "E1304", {"start": v(0.76, -11.89) * mm, "end": v(0.8, -11.77) * mm});
            skLineSegment(sketch, "E1305", {"start": v(0.8, -11.77) * mm, "end": v(0.83, -11.66) * mm});
            skLineSegment(sketch, "E1306", {"start": v(0.83, -11.66) * mm, "end": v(0.87, -11.55) * mm});
            skLineSegment(sketch, "E1307", {"start": v(0.87, -11.55) * mm, "end": v(0.9, -11.43) * mm});
            skLineSegment(sketch, "E1308", {"start": v(0.9, -11.43) * mm, "end": v(0.93, -11.32) * mm});
            skLineSegment(sketch, "E1309", {"start": v(0.93, -11.32) * mm, "end": v(0.96, -11.2) * mm});
            skLineSegment(sketch, "E1310", {"start": v(0.96, -11.2) * mm, "end": v(1, -11.09) * mm});
            skLineSegment(sketch, "E1311", {"start": v(1, -11.09) * mm, "end": v(1.02, -10.98) * mm});
            skLineSegment(sketch, "E1312", {"start": v(1.02, -10.98) * mm, "end": v(1.04, -10.86) * mm});
            skLineSegment(sketch, "E1313", {"start": v(1.04, -10.86) * mm, "end": v(1.06, -10.75) * mm});
            skLineSegment(sketch, "E1314", {"start": v(1.06, -10.75) * mm, "end": v(1.08, -10.63) * mm});
            skLineSegment(sketch, "E1315", {"start": v(1.08, -10.63) * mm, "end": v(1.1, -10.52) * mm});
            skLineSegment(sketch, "E1316", {"start": v(1.1, -10.52) * mm, "end": v(1.11, -10.4) * mm});
            skLineSegment(sketch, "E1317", {"start": v(1.11, -10.4) * mm, "end": v(1.13, -10.29) * mm});
            skLineSegment(sketch, "E1318", {"start": v(1.13, -10.29) * mm, "end": v(1.14, -10.17) * mm});
            skLineSegment(sketch, "E1319", {"start": v(1.14, -10.17) * mm, "end": v(1.15, -10.06) * mm});
            skLineSegment(sketch, "E1320", {"start": v(1.15, -10.06) * mm, "end": v(1.15, -9.94) * mm});
            skLineSegment(sketch, "E1321", {"start": v(1.15, -9.94) * mm, "end": v(1.16, -9.83) * mm});
            skLineSegment(sketch, "E1322", {"start": v(1.16, -9.83) * mm, "end": v(1.16, -9.71) * mm});
            skLineSegment(sketch, "E1323", {"start": v(1.16, -9.71) * mm, "end": v(1.16, -9.6) * mm});
            skLineSegment(sketch, "E1324", {"start": v(1.16, -9.6) * mm, "end": v(1.16, -9.48) * mm});
            skLineSegment(sketch, "E1325", {"start": v(1.16, -9.48) * mm, "end": v(1.16, -9.37) * mm});
            skLineSegment(sketch, "E1326", {"start": v(1.16, -9.37) * mm, "end": v(1.15, -9.26) * mm});
            skLineSegment(sketch, "E1327", {"start": v(1.15, -9.26) * mm, "end": v(1.15, -9.14) * mm});
            skLineSegment(sketch, "E1328", {"start": v(1.15, -9.14) * mm, "end": v(1.14, -9.03) * mm});
            skLineSegment(sketch, "E1329", {"start": v(1.14, -9.03) * mm, "end": v(1.13, -8.92) * mm});
            skLineSegment(sketch, "E1330", {"start": v(1.13, -8.92) * mm, "end": v(1.11, -8.8) * mm});
            skLineSegment(sketch, "E1331", {"start": v(1.11, -8.8) * mm, "end": v(1.1, -8.7) * mm});
            skLineSegment(sketch, "E1332", {"start": v(1.1, -8.7) * mm, "end": v(1.08, -8.58) * mm});
            skLineSegment(sketch, "E1333", {"start": v(1.08, -8.58) * mm, "end": v(1.06, -8.47) * mm});
            skLineSegment(sketch, "E1334", {"start": v(1.06, -8.47) * mm, "end": v(1.04, -8.35) * mm});
            skLineSegment(sketch, "E1335", {"start": v(1.04, -8.35) * mm, "end": v(1.02, -8.24) * mm});
            skLineSegment(sketch, "E1336", {"start": v(1.02, -8.24) * mm, "end": v(1, -8.13) * mm});
            skLineSegment(sketch, "E1337", {"start": v(1, -8.13) * mm, "end": v(0.97, -8.02) * mm});
            skLineSegment(sketch, "E1338", {"start": v(0.97, -8.02) * mm, "end": v(0.94, -7.9) * mm});
            skLineSegment(sketch, "E1339", {"start": v(0.94, -7.9) * mm, "end": v(0.9, -7.8) * mm});
            skLineSegment(sketch, "E1340", {"start": v(0.9, -7.8) * mm, "end": v(0.88, -7.68) * mm});
            skLineSegment(sketch, "E1341", {"start": v(0.88, -7.68) * mm, "end": v(0.84, -7.57) * mm});
            skLineSegment(sketch, "E1342", {"start": v(0.84, -7.57) * mm, "end": v(0.8, -7.45) * mm});
            skLineSegment(sketch, "E1343", {"start": v(0.8, -7.45) * mm, "end": v(0.77, -7.34) * mm});
            skLineSegment(sketch, "E1344", {"start": v(0.77, -7.34) * mm, "end": v(0.73, -7.23) * mm});
            skLineSegment(sketch, "E1345", {"start": v(0.73, -7.23) * mm, "end": v(0.69, -7.12) * mm});
            skLineSegment(sketch, "E1346", {"start": v(0.69, -7.12) * mm, "end": v(0.64, -7) * mm});
            skLineSegment(sketch, "E1347", {"start": v(0.64, -7) * mm, "end": v(0.6, -6.9) * mm});
            skLineSegment(sketch, "E1348", {"start": v(0.6, -6.9) * mm, "end": v(0.55, -6.78) * mm});
            skLineSegment(sketch, "E1349", {"start": v(0.55, -6.78) * mm, "end": v(0.5, -6.67) * mm});
            skLineSegment(sketch, "E1350", {"start": v(0.5, -6.67) * mm, "end": v(0.44, -6.56) * mm});
            skLineSegment(sketch, "E1351", {"start": v(0.44, -6.56) * mm, "end": v(0.4, -6.44) * mm});
            skLineSegment(sketch, "E1352", {"start": v(0.4, -6.44) * mm, "end": v(0.33, -6.33) * mm});
            skLineSegment(sketch, "E1353", {"start": v(0.33, -6.33) * mm, "end": v(0.28, -6.22) * mm});
            skLineSegment(sketch, "E1354", {"start": v(0.28, -6.22) * mm, "end": v(0.26, -6.2) * mm});
            skLineSegment(sketch, "E1355", {"start": v(0.26, -6.2) * mm, "end": v(-0.34, -6.2) * mm});
            skLineSegment(sketch, "E1356", {"start": v(-0.34, -6.2) * mm, "end": v(-0.35, -6.2) * mm});
            skLineSegment(sketch, "E1357", {"start": v(-0.35, -6.2) * mm, "end": v(-0.4, -6.31) * mm});
            skLineSegment(sketch, "E1358", {"start": v(-0.4, -6.31) * mm, "end": v(-0.45, -6.42) * mm});
            skLineSegment(sketch, "E1359", {"start": v(-0.45, -6.42) * mm, "end": v(-0.5, -6.54) * mm});
            skLineSegment(sketch, "E1360", {"start": v(-0.5, -6.54) * mm, "end": v(-0.54, -6.65) * mm});
            skLineSegment(sketch, "E1361", {"start": v(-0.54, -6.65) * mm, "end": v(-0.58, -6.76) * mm});
            skLineSegment(sketch, "E1362", {"start": v(-0.58, -6.76) * mm, "end": v(-0.62, -6.87) * mm});
            skLineSegment(sketch, "E1363", {"start": v(-0.62, -6.87) * mm, "end": v(-0.66, -6.99) * mm});
            skLineSegment(sketch, "E1364", {"start": v(-0.66, -6.99) * mm, "end": v(-0.7, -7.1) * mm});
            skLineSegment(sketch, "E1365", {"start": v(-0.7, -7.1) * mm, "end": v(-0.74, -7.21) * mm});
            skLineSegment(sketch, "E1366", {"start": v(-0.74, -7.21) * mm, "end": v(-0.77, -7.33) * mm});
            skLineSegment(sketch, "E1367", {"start": v(-0.77, -7.33) * mm, "end": v(-0.8, -7.44) * mm});
            skLineSegment(sketch, "E1368", {"start": v(-0.8, -7.44) * mm, "end": v(-0.84, -7.55) * mm});
            skLineSegment(sketch, "E1369", {"start": v(-0.84, -7.55) * mm, "end": v(-0.87, -7.66) * mm});
            skLineSegment(sketch, "E1370", {"start": v(-0.87, -7.66) * mm, "end": v(-0.9, -7.78) * mm});
            skLineSegment(sketch, "E1371", {"start": v(-0.9, -7.78) * mm, "end": v(-0.92, -7.9) * mm});
            skLineSegment(sketch, "E1372", {"start": v(-0.92, -7.9) * mm, "end": v(-0.95, -8) * mm});
            skLineSegment(sketch, "E1373", {"start": v(-0.95, -8) * mm, "end": v(-0.97, -8.12) * mm});
            skLineSegment(sketch, "E1374", {"start": v(-0.97, -8.12) * mm, "end": v(-1, -8.23) * mm});
            skLineSegment(sketch, "E1375", {"start": v(-1, -8.23) * mm, "end": v(-1.01, -8.34) * mm});
            skLineSegment(sketch, "E1376", {"start": v(-1.01, -8.34) * mm, "end": v(-1.03, -8.46) * mm});
            skLineSegment(sketch, "E1377", {"start": v(-1.03, -8.46) * mm, "end": v(-1.04, -8.57) * mm});
            skLineSegment(sketch, "E1378", {"start": v(-1.04, -8.57) * mm, "end": v(-1.06, -8.69) * mm});
            skLineSegment(sketch, "E1379", {"start": v(-1.06, -8.69) * mm, "end": v(-1.07, -8.8) * mm});
            skLineSegment(sketch, "E1380", {"start": v(-1.07, -8.8) * mm, "end": v(-1.08, -8.91) * mm});
            skLineSegment(sketch, "E1381", {"start": v(-1.08, -8.91) * mm, "end": v(-1.1, -9.03) * mm});
            skLineSegment(sketch, "E1382", {"start": v(-1.1, -9.03) * mm, "end": v(-1.1, -9.14) * mm});
            skLineSegment(sketch, "E1383", {"start": v(-1.1, -9.14) * mm, "end": v(-1.1, -9.26) * mm});
            skLineSegment(sketch, "E1384", {"start": v(-1.1, -9.26) * mm, "end": v(-1.11, -9.37) * mm});
            skLineSegment(sketch, "E1385", {"start": v(-1.11, -9.37) * mm, "end": v(-1.11, -9.48) * mm});
            skLineSegment(sketch, "E1386", {"start": v(-1.11, -9.48) * mm, "end": v(-1.11, -9.6) * mm});
            skLineSegment(sketch, "E1387", {"start": v(-1.11, -9.6) * mm, "end": v(-1.11, -9.71) * mm});
            skLineSegment(sketch, "E1388", {"start": v(-1.11, -9.71) * mm, "end": v(-1.11, -9.83) * mm});
            skLineSegment(sketch, "E1389", {"start": v(-1.11, -9.83) * mm, "end": v(-1.1, -9.95) * mm});
            skLineSegment(sketch, "E1390", {"start": v(-1.1, -9.95) * mm, "end": v(-1.1, -10.06) * mm});
            skLineSegment(sketch, "E1391", {"start": v(-1.1, -10.06) * mm, "end": v(-1.1, -10.18) * mm});
            skLineSegment(sketch, "E1392", {"start": v(-1.1, -10.18) * mm, "end": v(-1.08, -10.3) * mm});
            skLineSegment(sketch, "E1393", {"start": v(-1.08, -10.3) * mm, "end": v(-1.07, -10.4) * mm});
            skLineSegment(sketch, "E1394", {"start": v(-1.07, -10.4) * mm, "end": v(-1.06, -10.52) * mm});
            skLineSegment(sketch, "E1395", {"start": v(-1.06, -10.52) * mm, "end": v(-1.04, -10.64) * mm});
            skLineSegment(sketch, "E1396", {"start": v(-1.04, -10.64) * mm, "end": v(-1.03, -10.75) * mm});
            skLineSegment(sketch, "E1397", {"start": v(-1.03, -10.75) * mm, "end": v(-1, -10.87) * mm});
            skLineSegment(sketch, "E1398", {"start": v(-1, -10.87) * mm, "end": v(-0.99, -10.99) * mm});
            skLineSegment(sketch, "E1399", {"start": v(-0.99, -10.99) * mm, "end": v(-0.96, -11.1) * mm});
            skLineSegment(sketch, "E1400", {"start": v(-0.96, -11.1) * mm, "end": v(-0.94, -11.22) * mm});
            skLineSegment(sketch, "E1401", {"start": v(-0.94, -11.22) * mm, "end": v(-0.92, -11.33) * mm});
            skLineSegment(sketch, "E1402", {"start": v(-0.92, -11.33) * mm, "end": v(-0.89, -11.44) * mm});
            skLineSegment(sketch, "E1403", {"start": v(-0.89, -11.44) * mm, "end": v(-0.86, -11.56) * mm});
            skLineSegment(sketch, "E1404", {"start": v(-0.86, -11.56) * mm, "end": v(-0.83, -11.67) * mm});
            skLineSegment(sketch, "E1405", {"start": v(-0.83, -11.67) * mm, "end": v(-0.8, -11.79) * mm});
            skLineSegment(sketch, "E1406", {"start": v(-0.8, -11.79) * mm, "end": v(-0.76, -11.9) * mm});
            skLineSegment(sketch, "E1407", {"start": v(-0.76, -11.9) * mm, "end": v(-0.73, -12.02) * mm});
            skLineSegment(sketch, "E1408", {"start": v(-0.73, -12.02) * mm, "end": v(-0.69, -12.13) * mm});
            skLineSegment(sketch, "E1409", {"start": v(-0.69, -12.13) * mm, "end": v(-0.65, -12.25) * mm});
            skLineSegment(sketch, "E1410", {"start": v(-0.65, -12.25) * mm, "end": v(-0.6, -12.36) * mm});
            skLineSegment(sketch, "E1411", {"start": v(-0.6, -12.36) * mm, "end": v(-0.57, -12.47) * mm});
            skLineSegment(sketch, "E1412", {"start": v(-0.57, -12.47) * mm, "end": v(-0.52, -12.59) * mm});
            skLineSegment(sketch, "E1413", {"start": v(-0.52, -12.59) * mm, "end": v(-0.48, -12.7) * mm});
            skLineSegment(sketch, "E1414", {"start": v(-0.48, -12.7) * mm, "end": v(-0.43, -12.82) * mm});
            skLineSegment(sketch, "E1415", {"start": v(-0.43, -12.82) * mm, "end": v(-0.38, -12.93) * mm});
            skLineSegment(sketch, "E1416", {"start": v(-0.38, -12.93) * mm, "end": v(-0.33, -13.04) * mm});
            skLineSegment(sketch, "E1417", {"start": v(-0.33, -13.04) * mm, "end": v(-0.32, -13.06) * mm});
            skLineSegment(sketch, "E1418", {"start": v(-0.32, -13.06) * mm, "end": v(0.23, -13.06) * mm});
            skLineSegment(sketch, "E1419", {"start": v(0.23, -13.06) * mm, "end": v(0.25, -13.03) * mm});
            skLineSegment(sketch, "E1420", {"start": v(0, 3) * mm, "end": v(0, -2.5) * mm, "construction": true});
            skLineSegment(sketch, "E1421", {"start": v(-1.66, -2.5) * mm, "end": v(1.66, -2.5) * mm});
            skPoint(sketch, "E1422", {"position": v(0, 0) * mm});
            skCircle(sketch, "E1423", {"center": v(0, 0) * mm, "radius": 1.5 * mm});
            skCircle(sketch, "E1424", {"center": v(0, 0) * mm, "radius": 3 * mm});
            skCircle(sketch, "E1425", {"center": v(0, 0) * mm, "radius": 4.5 * mm});
            skSolve(sketch);
        }
        {
            var Q0;
            Q0=makeQuery(id+"F0.imprint","IMPRINT",FACE,{"disambiguationData":[TD([[makeQuery(id+"F0.imprint","IMPRINT",EDGE,{"derivedFrom":sQuery(id+"F0.wireOp",EDGE,"E0")}),1.0]])]});
            var Q1;
            {var subQ4=sQuery(id+"F0.wireOp",EDGE,"E320");Q1=makeQuery(id+"F0.imprint","IMPRINT",FACE,{"disambiguationData":[TD([[makeQuery(id+"F0.imprint","IMPRINT",EDGE,{"derivedFrom":subQ4}),1.0]])]});}
            var Q2;
            {var subQ13=sQuery(id+"F0.wireOp",EDGE,"E320");Q2=makeQuery(id+"F0.imprint","IMPRINT",FACE,{"disambiguationData":[TD([[makeQuery(id+"F0.imprint","IMPRINT",EDGE,{"derivedFrom":subQ13}),-1.0]])]});}
            var Q3;
            {var subQ0=sQuery(id+"F0.wireOp",EDGE,"E507");Q3=makeQuery(id+"F0.imprint","IMPRINT",FACE,{"disambiguationData":[TD([[makeQuery(id+"F0.imprint","IMPRINT",EDGE,{"derivedFrom":subQ0}),1.0]])]});}
            var Q4;
            {var subQ4=sQuery(id+"F0.wireOp",EDGE,"E1024");Q4=makeQuery(id+"F0.imprint","IMPRINT",FACE,{"disambiguationData":[TD([[makeQuery(id+"F0.imprint","IMPRINT",EDGE,{"derivedFrom":subQ4}),1.0]])]});}
            var Q5;
            {var subQ0=sQuery(id+"F0.wireOp",EDGE,"E1211");Q5=makeQuery(id+"F0.imprint","IMPRINT",FACE,{"disambiguationData":[TD([[makeQuery(id+"F0.imprint","IMPRINT",EDGE,{"derivedFrom":subQ0}),1.0]])]});}
            var Q6;
            {var subQ0=sQuery(id+"F0.wireOp",EDGE,"E1421");Q6=makeQuery(id+"F0.imprint","IMPRINT",FACE,{"disambiguationData":[TD([[makeQuery(id+"F0.imprint","IMPRINT",EDGE,{"derivedFrom":subQ0}),-1.0]])]});}
            extrude(context, id + "F1", {"entities" : qUnion([Q0, Q1, Q2, Q3, Q4, Q5, Q6]), "depth" : 5 * mm});
        }
    });
